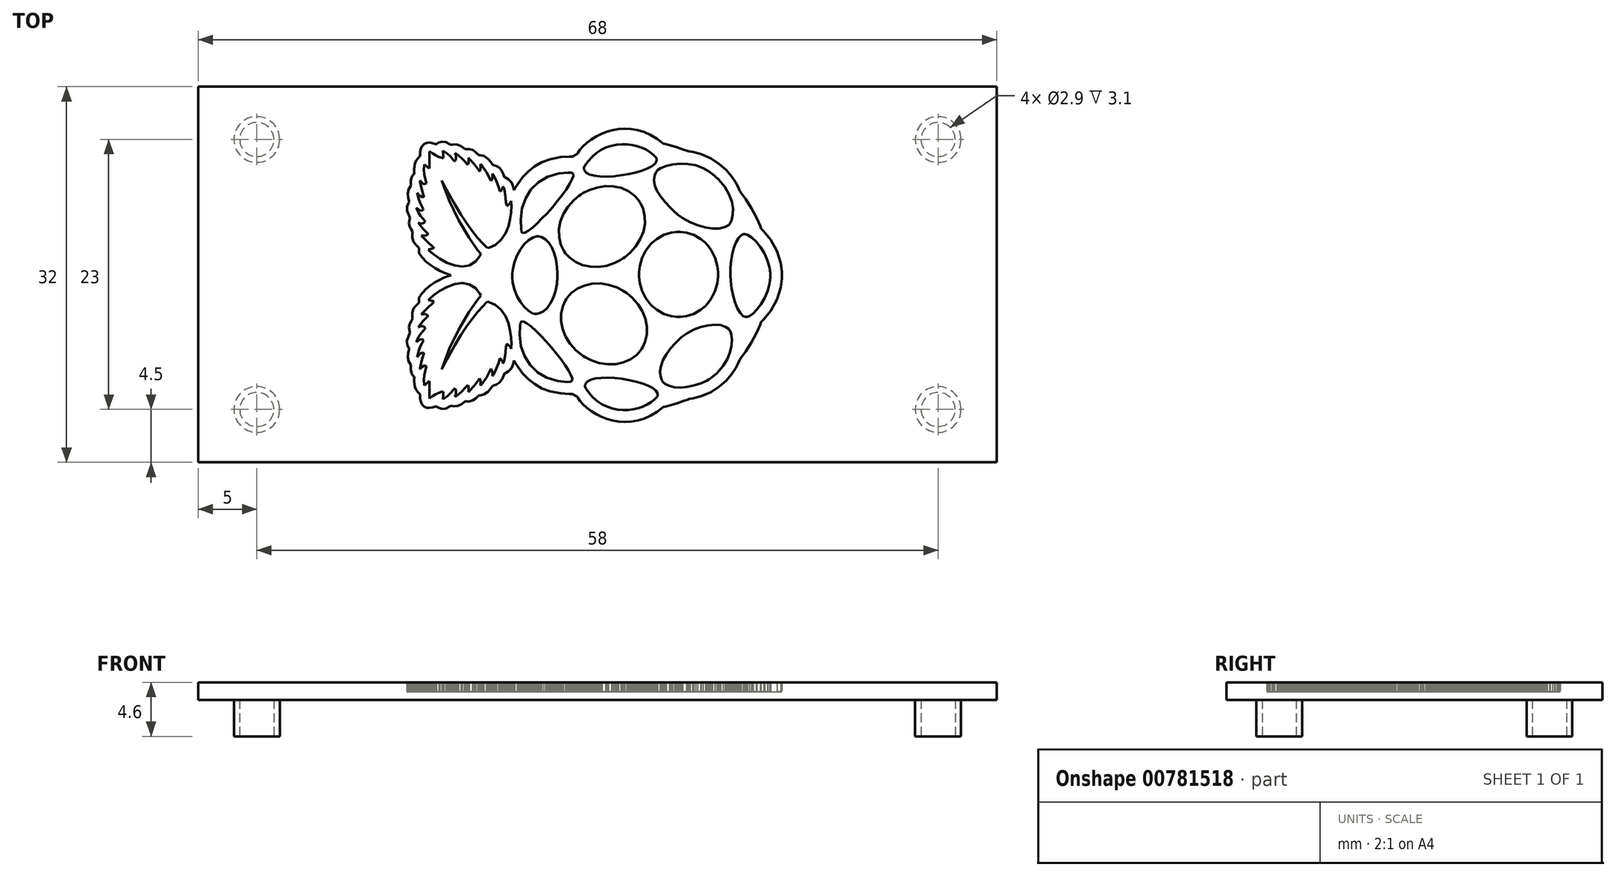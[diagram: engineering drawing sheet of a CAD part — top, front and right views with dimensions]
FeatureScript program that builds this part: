
annotation { "Feature Type Name" : "Feature", "Feature Type Description" : "" }
export const myFeature = defineFeature(function(context is Context, id is Id, definition is map)
    precondition{}
    {
        {
            var Q0;
            Q0=qCreatedBy(makeId("Top.planeOp"),FACE);
            var sketch = newSketch(context, id + "F0", { "sketchPlane" : qUnion([Q0])});
            skLineSegment(sketch, "E0.bottom", {"start": v(-34, 16) * mm, "end": v(34, 16) * mm});
            skLineSegment(sketch, "E0.top", {"start": v(-34, -16) * mm, "end": v(34, -16) * mm});
            skLineSegment(sketch, "E0.left", {"start": v(-34, 16) * mm, "end": v(-34, -16) * mm});
            skLineSegment(sketch, "E0.right", {"start": v(34, 16) * mm, "end": v(34, -16) * mm});
            skCircle(sketch, "E1", {"center": v(-29, 11.5) * mm, "radius": 1.45 * mm});
            skCircle(sketch, "E2", {"center": v(29, 11.5) * mm, "radius": 1.45 * mm});
            skCircle(sketch, "E3", {"center": v(29, -11.5) * mm, "radius": 1.45 * mm});
            skCircle(sketch, "E4", {"center": v(-29, -11.5) * mm, "radius": 1.45 * mm});
            skCircle(sketch, "E5", {"center": v(-29, 11.5) * mm, "radius": 1.95 * mm});
            skCircle(sketch, "E6", {"center": v(-29, -11.5) * mm, "radius": 1.95 * mm});
            skCircle(sketch, "E7", {"center": v(29, 11.5) * mm, "radius": 1.95 * mm});
            skCircle(sketch, "E8", {"center": v(29, -11.5) * mm, "radius": 1.95 * mm});
            skSolve(sketch);
        }
        {
            var Q0;
            Q0=qCreatedBy(makeId("Top.planeOp"),FACE);
            var sketch = newSketch(context, id + "F1", { "sketchPlane" : qUnion([Q0])});
            skLineSegment(sketch, "E9", {"start": v(-16.22, -5.8) * mm, "end": v(-16.22, -5.84) * mm});
            skLineSegment(sketch, "E10", {"start": v(-16.22, -5.84) * mm, "end": v(-16.17, -6.05) * mm});
            skLineSegment(sketch, "E11", {"start": v(-16.17, -6.05) * mm, "end": v(-16.04, -6.28) * mm});
            skLineSegment(sketch, "E12", {"start": v(-16.04, -6.28) * mm, "end": v(-16, -6.33) * mm});
            skLineSegment(sketch, "E13", {"start": v(-16, -6.33) * mm, "end": v(-16.04, -6.42) * mm});
            skLineSegment(sketch, "E14", {"start": v(-16.04, -6.42) * mm, "end": v(-16.12, -6.7) * mm});
            skLineSegment(sketch, "E15", {"start": v(-16.12, -6.7) * mm, "end": v(-16.15, -7.04) * mm});
            skLineSegment(sketch, "E16", {"start": v(-16.15, -7.04) * mm, "end": v(-16.08, -7.38) * mm});
            skLineSegment(sketch, "E17", {"start": v(-16.08, -7.38) * mm, "end": v(-15.94, -7.63) * mm});
            skLineSegment(sketch, "E18", {"start": v(-15.94, -7.63) * mm, "end": v(-15.87, -7.7) * mm});
            skLineSegment(sketch, "E19", {"start": v(-15.87, -7.7) * mm, "end": v(-15.89, -7.8) * mm});
            skLineSegment(sketch, "E20", {"start": v(-15.89, -7.8) * mm, "end": v(-15.9, -8.11) * mm});
            skLineSegment(sketch, "E21", {"start": v(-15.9, -8.11) * mm, "end": v(-15.84, -8.4) * mm});
            skLineSegment(sketch, "E22", {"start": v(-15.84, -8.4) * mm, "end": v(-15.73, -8.58) * mm});
            skLineSegment(sketch, "E23", {"start": v(-15.73, -8.58) * mm, "end": v(-15.62, -8.69) * mm});
            skLineSegment(sketch, "E24", {"start": v(-15.62, -8.69) * mm, "end": v(-15.58, -8.72) * mm});
            skLineSegment(sketch, "E25", {"start": v(-15.58, -8.72) * mm, "end": v(-15.58, -8.74) * mm});
            skLineSegment(sketch, "E26", {"start": v(-15.58, -8.74) * mm, "end": v(-15.59, -8.8) * mm});
            skLineSegment(sketch, "E27", {"start": v(-15.59, -8.8) * mm, "end": v(-15.6, -8.95) * mm});
            skLineSegment(sketch, "E28", {"start": v(-15.6, -8.95) * mm, "end": v(-15.6, -9.14) * mm});
            skLineSegment(sketch, "E29", {"start": v(-15.6, -9.14) * mm, "end": v(-15.58, -9.36) * mm});
            skLineSegment(sketch, "E30", {"start": v(-15.58, -9.36) * mm, "end": v(-15.53, -9.59) * mm});
            skLineSegment(sketch, "E31", {"start": v(-15.53, -9.59) * mm, "end": v(-15.44, -9.81) * mm});
            skLineSegment(sketch, "E32", {"start": v(-15.44, -9.81) * mm, "end": v(-15.3, -10.02) * mm});
            skLineSegment(sketch, "E33", {"start": v(-15.3, -10.02) * mm, "end": v(-15.16, -10.17) * mm});
            skLineSegment(sketch, "E34", {"start": v(-15.16, -10.17) * mm, "end": v(-15.1, -10.2) * mm});
            skLineSegment(sketch, "E35", {"start": v(-15.1, -10.2) * mm, "end": v(-15.11, -10.3) * mm});
            skLineSegment(sketch, "E36", {"start": v(-15.11, -10.3) * mm, "end": v(-15.1, -10.57) * mm});
            skLineSegment(sketch, "E37", {"start": v(-15.1, -10.57) * mm, "end": v(-15.04, -10.86) * mm});
            skLineSegment(sketch, "E38", {"start": v(-15.04, -10.86) * mm, "end": v(-14.92, -11.1) * mm});
            skLineSegment(sketch, "E39", {"start": v(-14.92, -11.1) * mm, "end": v(-14.75, -11.25) * mm});
            skLineSegment(sketch, "E40", {"start": v(-14.75, -11.25) * mm, "end": v(-14.54, -11.35) * mm});
            skLineSegment(sketch, "E41", {"start": v(-14.54, -11.35) * mm, "end": v(-14.3, -11.37) * mm});
            skLineSegment(sketch, "E42", {"start": v(-14.3, -11.37) * mm, "end": v(-14.04, -11.33) * mm});
            skLineSegment(sketch, "E43", {"start": v(-14.04, -11.33) * mm, "end": v(-13.84, -11.25) * mm});
            skLineSegment(sketch, "E44", {"start": v(-13.84, -11.25) * mm, "end": v(-13.78, -11.22) * mm});
            skLineSegment(sketch, "E45", {"start": v(-13.78, -11.22) * mm, "end": v(-13.71, -11.26) * mm});
            skLineSegment(sketch, "E46", {"start": v(-13.71, -11.26) * mm, "end": v(-13.52, -11.37) * mm});
            skLineSegment(sketch, "E47", {"start": v(-13.52, -11.37) * mm, "end": v(-13.24, -11.46) * mm});
            skLineSegment(sketch, "E48", {"start": v(-13.24, -11.46) * mm, "end": v(-12.9, -11.4) * mm});
            skLineSegment(sketch, "E49", {"start": v(-12.9, -11.4) * mm, "end": v(-12.57, -11.23) * mm});
            skLineSegment(sketch, "E50", {"start": v(-12.57, -11.23) * mm, "end": v(-12.47, -11.15) * mm});
            skLineSegment(sketch, "E51", {"start": v(-12.47, -11.15) * mm, "end": v(-12.4, -11.19) * mm});
            skLineSegment(sketch, "E52", {"start": v(-12.4, -11.19) * mm, "end": v(-12.2, -11.23) * mm});
            skLineSegment(sketch, "E53", {"start": v(-12.2, -11.23) * mm, "end": v(-11.9, -11.2) * mm});
            skLineSegment(sketch, "E54", {"start": v(-11.9, -11.2) * mm, "end": v(-11.6, -11.06) * mm});
            skLineSegment(sketch, "E55", {"start": v(-11.6, -11.06) * mm, "end": v(-11.34, -10.87) * mm});
            skLineSegment(sketch, "E56", {"start": v(-11.34, -10.87) * mm, "end": v(-11.26, -10.8) * mm});
            skLineSegment(sketch, "E57", {"start": v(-11.26, -10.8) * mm, "end": v(-11.18, -10.82) * mm});
            skLineSegment(sketch, "E58", {"start": v(-11.18, -10.82) * mm, "end": v(-10.91, -10.82) * mm});
            skLineSegment(sketch, "E59", {"start": v(-10.91, -10.82) * mm, "end": v(-10.61, -10.74) * mm});
            skLineSegment(sketch, "E60", {"start": v(-10.61, -10.74) * mm, "end": v(-10.35, -10.56) * mm});
            skLineSegment(sketch, "E61", {"start": v(-10.35, -10.56) * mm, "end": v(-10.18, -10.37) * mm});
            skLineSegment(sketch, "E62", {"start": v(-10.18, -10.37) * mm, "end": v(-10.13, -10.3) * mm});
            skLineSegment(sketch, "E63", {"start": v(-10.13, -10.3) * mm, "end": v(-10.02, -10.31) * mm});
            skLineSegment(sketch, "E64", {"start": v(-10.02, -10.31) * mm, "end": v(-9.67, -10.23) * mm});
            skLineSegment(sketch, "E65", {"start": v(-9.67, -10.23) * mm, "end": v(-9.32, -9.99) * mm});
            skLineSegment(sketch, "E66", {"start": v(-9.32, -9.99) * mm, "end": v(-9.06, -9.7) * mm});
            skLineSegment(sketch, "E67", {"start": v(-9.06, -9.7) * mm, "end": v(-8.94, -9.51) * mm});
            skLineSegment(sketch, "E68", {"start": v(-8.94, -9.51) * mm, "end": v(-8.9, -9.46) * mm});
            skLineSegment(sketch, "E69", {"start": v(-8.9, -9.46) * mm, "end": v(-8.83, -9.45) * mm});
            skLineSegment(sketch, "E70", {"start": v(-8.83, -9.45) * mm, "end": v(-8.61, -9.38) * mm});
            skLineSegment(sketch, "E71", {"start": v(-8.61, -9.38) * mm, "end": v(-8.34, -9.2) * mm});
            skLineSegment(sketch, "E72", {"start": v(-8.34, -9.2) * mm, "end": v(-8.1, -8.9) * mm});
            skLineSegment(sketch, "E73", {"start": v(-8.1, -8.9) * mm, "end": v(-7.96, -8.54) * mm});
            skLineSegment(sketch, "E74", {"start": v(-7.96, -8.54) * mm, "end": v(-7.92, -8.41) * mm});
            skLineSegment(sketch, "E75", {"start": v(-7.92, -8.41) * mm, "end": v(-7.83, -8.4) * mm});
            skLineSegment(sketch, "E76", {"start": v(-7.83, -8.4) * mm, "end": v(-7.56, -8.25) * mm});
            skLineSegment(sketch, "E77", {"start": v(-7.56, -8.25) * mm, "end": v(-7.33, -8) * mm});
            skLineSegment(sketch, "E78", {"start": v(-7.33, -8) * mm, "end": v(-7.2, -7.68) * mm});
            skLineSegment(sketch, "E79", {"start": v(-7.2, -7.68) * mm, "end": v(-7.12, -7.42) * mm});
            skLineSegment(sketch, "E80", {"start": v(-7.12, -7.42) * mm, "end": v(-7.1, -7.33) * mm});
            skLineSegment(sketch, "E81", {"start": v(-7.1, -7.33) * mm, "end": v(-7.02, -7.48) * mm});
            skLineSegment(sketch, "E82", {"start": v(-7.02, -7.48) * mm, "end": v(-6.75, -7.9) * mm});
            skLineSegment(sketch, "E83", {"start": v(-6.75, -7.9) * mm, "end": v(-6.35, -8.43) * mm});
            skLineSegment(sketch, "E84", {"start": v(-6.35, -8.43) * mm, "end": v(-5.9, -8.92) * mm});
            skLineSegment(sketch, "E85", {"start": v(-5.9, -8.92) * mm, "end": v(-5.36, -9.34) * mm});
            skLineSegment(sketch, "E86", {"start": v(-5.36, -9.34) * mm, "end": v(-4.74, -9.7) * mm});
            skLineSegment(sketch, "E87", {"start": v(-4.74, -9.7) * mm, "end": v(-4, -9.96) * mm});
            skLineSegment(sketch, "E88", {"start": v(-4, -9.96) * mm, "end": v(-3.14, -10.13) * mm});
            skLineSegment(sketch, "E89", {"start": v(-3.14, -10.13) * mm, "end": v(-2.38, -10.19) * mm});
            skLineSegment(sketch, "E90", {"start": v(-2.38, -10.19) * mm, "end": v(-2.13, -10.19) * mm});
            skLineSegment(sketch, "E91", {"start": v(-2.13, -10.19) * mm, "end": v(-1.73, -10.41) * mm});
            skLineSegment(sketch, "E92", {"start": v(-1.73, -10.41) * mm, "end": v(-1.68, -10.5) * mm});
            skLineSegment(sketch, "E93", {"start": v(-1.68, -10.5) * mm, "end": v(-1.5, -10.74) * mm});
            skLineSegment(sketch, "E94", {"start": v(-1.5, -10.74) * mm, "end": v(-1.22, -11.06) * mm});
            skLineSegment(sketch, "E95", {"start": v(-1.22, -11.06) * mm, "end": v(-0.9, -11.36) * mm});
            skLineSegment(sketch, "E96", {"start": v(-0.9, -11.36) * mm, "end": v(-0.52, -11.64) * mm});
            skLineSegment(sketch, "E97", {"start": v(-0.52, -11.64) * mm, "end": v(-0.12, -11.9) * mm});
            skLineSegment(sketch, "E98", {"start": v(-0.12, -11.9) * mm, "end": v(0.33, -12.12) * mm});
            skLineSegment(sketch, "E99", {"start": v(0.33, -12.12) * mm, "end": v(0.8, -12.3) * mm});
            skLineSegment(sketch, "E100", {"start": v(0.8, -12.3) * mm, "end": v(1.3, -12.44) * mm});
            skLineSegment(sketch, "E101", {"start": v(1.3, -12.44) * mm, "end": v(1.8, -12.53) * mm});
            skLineSegment(sketch, "E102", {"start": v(1.8, -12.53) * mm, "end": v(2.34, -12.57) * mm});
            skLineSegment(sketch, "E103", {"start": v(2.34, -12.57) * mm, "end": v(2.88, -12.54) * mm});
            skLineSegment(sketch, "E104", {"start": v(2.88, -12.54) * mm, "end": v(3.43, -12.45) * mm});
            skLineSegment(sketch, "E105", {"start": v(3.43, -12.45) * mm, "end": v(3.98, -12.28) * mm});
            skLineSegment(sketch, "E106", {"start": v(3.98, -12.28) * mm, "end": v(4.53, -12.03) * mm});
            skLineSegment(sketch, "E107", {"start": v(4.53, -12.03) * mm, "end": v(5.08, -11.7) * mm});
            skLineSegment(sketch, "E108", {"start": v(5.08, -11.7) * mm, "end": v(5.48, -11.4) * mm});
            skLineSegment(sketch, "E109", {"start": v(5.48, -11.4) * mm, "end": v(5.61, -11.28) * mm});
            skLineSegment(sketch, "E110", {"start": v(5.61, -11.28) * mm, "end": v(5.77, -11.26) * mm});
            skLineSegment(sketch, "E111", {"start": v(5.77, -11.26) * mm, "end": v(6.23, -11.14) * mm});
            skLineSegment(sketch, "E112", {"start": v(6.23, -11.14) * mm, "end": v(6.78, -10.98) * mm});
            skLineSegment(sketch, "E113", {"start": v(6.78, -10.98) * mm, "end": v(7.3, -10.8) * mm});
            skLineSegment(sketch, "E114", {"start": v(7.3, -10.8) * mm, "end": v(7.69, -10.65) * mm});
            skLineSegment(sketch, "E115", {"start": v(7.69, -10.65) * mm, "end": v(7.82, -10.6) * mm});
            skLineSegment(sketch, "E116", {"start": v(7.82, -10.6) * mm, "end": v(8.07, -10.57) * mm});
            skLineSegment(sketch, "E117", {"start": v(8.07, -10.57) * mm, "end": v(8.8, -10.38) * mm});
            skLineSegment(sketch, "E118", {"start": v(8.8, -10.38) * mm, "end": v(9.66, -10.02) * mm});
            skLineSegment(sketch, "E119", {"start": v(9.66, -10.02) * mm, "end": v(10.37, -9.55) * mm});
            skLineSegment(sketch, "E120", {"start": v(10.37, -9.55) * mm, "end": v(10.96, -9.03) * mm});
            skLineSegment(sketch, "E121", {"start": v(10.96, -9.03) * mm, "end": v(11.43, -8.5) * mm});
            skLineSegment(sketch, "E122", {"start": v(11.43, -8.5) * mm, "end": v(11.77, -7.99) * mm});
            skLineSegment(sketch, "E123", {"start": v(11.77, -7.99) * mm, "end": v(12, -7.56) * mm});
            skLineSegment(sketch, "E124", {"start": v(12, -7.56) * mm, "end": v(12.1, -7.33) * mm});
            skLineSegment(sketch, "E125", {"start": v(12.1, -7.33) * mm, "end": v(12.11, -7.25) * mm});
            skLineSegment(sketch, "E126", {"start": v(12.11, -7.25) * mm, "end": v(12.24, -7.08) * mm});
            skLineSegment(sketch, "E127", {"start": v(12.24, -7.08) * mm, "end": v(12.62, -6.55) * mm});
            skLineSegment(sketch, "E128", {"start": v(12.62, -6.55) * mm, "end": v(13.1, -5.8) * mm});
            skLineSegment(sketch, "E129", {"start": v(13.1, -5.8) * mm, "end": v(13.55, -4.97) * mm});
            skLineSegment(sketch, "E130", {"start": v(13.55, -4.97) * mm, "end": v(13.85, -4.28) * mm});
            skLineSegment(sketch, "E131", {"start": v(13.85, -4.28) * mm, "end": v(13.93, -4.04) * mm});
            skLineSegment(sketch, "E132", {"start": v(13.93, -4.04) * mm, "end": v(14.16, -3.83) * mm});
            skLineSegment(sketch, "E133", {"start": v(14.16, -3.83) * mm, "end": v(14.75, -3.1) * mm});
            skLineSegment(sketch, "E134", {"start": v(14.75, -3.1) * mm, "end": v(15.3, -2.11) * mm});
            skLineSegment(sketch, "E135", {"start": v(15.3, -2.11) * mm, "end": v(15.6, -1.11) * mm});
            skLineSegment(sketch, "E136", {"start": v(15.6, -1.11) * mm, "end": v(15.7, -0.35) * mm});
            skLineSegment(sketch, "E137", {"start": v(15.7, -0.35) * mm, "end": v(15.7, -0.1) * mm});
            skLineSegment(sketch, "E138", {"start": v(15.7, -0.1) * mm, "end": v(15.7, -0.08) * mm});
            skLineSegment(sketch, "E139", {"start": v(15.7, -0.08) * mm, "end": v(15.7, -0.04) * mm});
            skLineSegment(sketch, "E140", {"start": v(15.7, -0.04) * mm, "end": v(15.7, -0.04) * mm});
            skLineSegment(sketch, "E141", {"start": v(15.7, -0.04) * mm, "end": v(15.7, 0.22) * mm});
            skLineSegment(sketch, "E142", {"start": v(15.7, 0.22) * mm, "end": v(15.6, 0.98) * mm});
            skLineSegment(sketch, "E143", {"start": v(15.6, 0.98) * mm, "end": v(15.3, 1.98) * mm});
            skLineSegment(sketch, "E144", {"start": v(15.3, 1.98) * mm, "end": v(14.75, 2.96) * mm});
            skLineSegment(sketch, "E145", {"start": v(14.75, 2.96) * mm, "end": v(14.16, 3.7) * mm});
            skLineSegment(sketch, "E146", {"start": v(14.16, 3.7) * mm, "end": v(13.93, 3.9) * mm});
            skLineSegment(sketch, "E147", {"start": v(13.93, 3.9) * mm, "end": v(13.85, 4.14) * mm});
            skLineSegment(sketch, "E148", {"start": v(13.85, 4.14) * mm, "end": v(13.55, 4.84) * mm});
            skLineSegment(sketch, "E149", {"start": v(13.55, 4.84) * mm, "end": v(13.1, 5.66) * mm});
            skLineSegment(sketch, "E150", {"start": v(13.1, 5.66) * mm, "end": v(12.62, 6.41) * mm});
            skLineSegment(sketch, "E151", {"start": v(12.62, 6.41) * mm, "end": v(12.24, 6.94) * mm});
            skLineSegment(sketch, "E152", {"start": v(12.24, 6.94) * mm, "end": v(12.11, 7.12) * mm});
            skLineSegment(sketch, "E153", {"start": v(12.11, 7.12) * mm, "end": v(12.1, 7.2) * mm});
            skLineSegment(sketch, "E154", {"start": v(12.1, 7.2) * mm, "end": v(12, 7.42) * mm});
            skLineSegment(sketch, "E155", {"start": v(12, 7.42) * mm, "end": v(11.77, 7.85) * mm});
            skLineSegment(sketch, "E156", {"start": v(11.77, 7.85) * mm, "end": v(11.43, 8.36) * mm});
            skLineSegment(sketch, "E157", {"start": v(11.43, 8.36) * mm, "end": v(10.96, 8.9) * mm});
            skLineSegment(sketch, "E158", {"start": v(10.96, 8.9) * mm, "end": v(10.37, 9.42) * mm});
            skLineSegment(sketch, "E159", {"start": v(10.37, 9.42) * mm, "end": v(9.66, 9.88) * mm});
            skLineSegment(sketch, "E160", {"start": v(9.66, 9.88) * mm, "end": v(8.8, 10.25) * mm});
            skLineSegment(sketch, "E161", {"start": v(8.8, 10.25) * mm, "end": v(8.07, 10.44) * mm});
            skLineSegment(sketch, "E162", {"start": v(8.07, 10.44) * mm, "end": v(7.82, 10.47) * mm});
            skLineSegment(sketch, "E163", {"start": v(7.82, 10.47) * mm, "end": v(7.69, 10.52) * mm});
            skLineSegment(sketch, "E164", {"start": v(7.69, 10.52) * mm, "end": v(7.3, 10.66) * mm});
            skLineSegment(sketch, "E165", {"start": v(7.3, 10.66) * mm, "end": v(6.78, 10.84) * mm});
            skLineSegment(sketch, "E166", {"start": v(6.78, 10.84) * mm, "end": v(6.23, 11) * mm});
            skLineSegment(sketch, "E167", {"start": v(6.23, 11) * mm, "end": v(5.77, 11.12) * mm});
            skLineSegment(sketch, "E168", {"start": v(5.77, 11.12) * mm, "end": v(5.61, 11.15) * mm});
            skLineSegment(sketch, "E169", {"start": v(5.61, 11.15) * mm, "end": v(5.48, 11.26) * mm});
            skLineSegment(sketch, "E170", {"start": v(5.48, 11.26) * mm, "end": v(5.08, 11.57) * mm});
            skLineSegment(sketch, "E171", {"start": v(5.08, 11.57) * mm, "end": v(4.53, 11.9) * mm});
            skLineSegment(sketch, "E172", {"start": v(4.53, 11.9) * mm, "end": v(3.98, 12.14) * mm});
            skLineSegment(sketch, "E173", {"start": v(3.98, 12.14) * mm, "end": v(3.43, 12.31) * mm});
            skLineSegment(sketch, "E174", {"start": v(3.43, 12.31) * mm, "end": v(2.88, 12.4) * mm});
            skLineSegment(sketch, "E175", {"start": v(2.88, 12.4) * mm, "end": v(2.34, 12.43) * mm});
            skLineSegment(sketch, "E176", {"start": v(2.34, 12.43) * mm, "end": v(1.8, 12.4) * mm});
            skLineSegment(sketch, "E177", {"start": v(1.8, 12.4) * mm, "end": v(1.3, 12.3) * mm});
            skLineSegment(sketch, "E178", {"start": v(1.3, 12.3) * mm, "end": v(0.8, 12.17) * mm});
            skLineSegment(sketch, "E179", {"start": v(0.8, 12.17) * mm, "end": v(0.32, 11.99) * mm});
            skLineSegment(sketch, "E180", {"start": v(0.32, 11.99) * mm, "end": v(-0.12, 11.76) * mm});
            skLineSegment(sketch, "E181", {"start": v(-0.12, 11.76) * mm, "end": v(-0.52, 11.5) * mm});
            skLineSegment(sketch, "E182", {"start": v(-0.52, 11.5) * mm, "end": v(-0.9, 11.23) * mm});
            skLineSegment(sketch, "E183", {"start": v(-0.9, 11.23) * mm, "end": v(-1.22, 10.92) * mm});
            skLineSegment(sketch, "E184", {"start": v(-1.22, 10.92) * mm, "end": v(-1.5, 10.6) * mm});
            skLineSegment(sketch, "E185", {"start": v(-1.5, 10.6) * mm, "end": v(-1.68, 10.36) * mm});
            skLineSegment(sketch, "E186", {"start": v(-1.68, 10.36) * mm, "end": v(-1.73, 10.28) * mm});
            skLineSegment(sketch, "E187", {"start": v(-1.73, 10.28) * mm, "end": v(-2.13, 10.05) * mm});
            skLineSegment(sketch, "E188", {"start": v(-2.13, 10.05) * mm, "end": v(-2.38, 10.05) * mm});
            skLineSegment(sketch, "E189", {"start": v(-2.38, 10.05) * mm, "end": v(-3.14, 10) * mm});
            skLineSegment(sketch, "E190", {"start": v(-3.14, 10) * mm, "end": v(-4, 9.83) * mm});
            skLineSegment(sketch, "E191", {"start": v(-4, 9.83) * mm, "end": v(-4.74, 9.56) * mm});
            skLineSegment(sketch, "E192", {"start": v(-4.74, 9.56) * mm, "end": v(-5.36, 9.2) * mm});
            skLineSegment(sketch, "E193", {"start": v(-5.36, 9.2) * mm, "end": v(-5.9, 8.78) * mm});
            skLineSegment(sketch, "E194", {"start": v(-5.9, 8.78) * mm, "end": v(-6.35, 8.3) * mm});
            skLineSegment(sketch, "E195", {"start": v(-6.35, 8.3) * mm, "end": v(-6.75, 7.76) * mm});
            skLineSegment(sketch, "E196", {"start": v(-6.75, 7.76) * mm, "end": v(-7.02, 7.34) * mm});
            skLineSegment(sketch, "E197", {"start": v(-7.02, 7.34) * mm, "end": v(-7.1, 7.2) * mm});
            skLineSegment(sketch, "E198", {"start": v(-7.1, 7.2) * mm, "end": v(-7.12, 7.28) * mm});
            skLineSegment(sketch, "E199", {"start": v(-7.12, 7.28) * mm, "end": v(-7.2, 7.54) * mm});
            skLineSegment(sketch, "E200", {"start": v(-7.2, 7.54) * mm, "end": v(-7.34, 7.86) * mm});
            skLineSegment(sketch, "E201", {"start": v(-7.34, 7.86) * mm, "end": v(-7.56, 8.12) * mm});
            skLineSegment(sketch, "E202", {"start": v(-7.56, 8.12) * mm, "end": v(-7.83, 8.26) * mm});
            skLineSegment(sketch, "E203", {"start": v(-7.83, 8.26) * mm, "end": v(-7.92, 8.28) * mm});
            skLineSegment(sketch, "E204", {"start": v(-7.92, 8.28) * mm, "end": v(-7.96, 8.4) * mm});
            skLineSegment(sketch, "E205", {"start": v(-7.96, 8.4) * mm, "end": v(-8.1, 8.77) * mm});
            skLineSegment(sketch, "E206", {"start": v(-8.1, 8.77) * mm, "end": v(-8.34, 9.07) * mm});
            skLineSegment(sketch, "E207", {"start": v(-8.34, 9.07) * mm, "end": v(-8.61, 9.24) * mm});
            skLineSegment(sketch, "E208", {"start": v(-8.61, 9.24) * mm, "end": v(-8.83, 9.31) * mm});
            skLineSegment(sketch, "E209", {"start": v(-8.83, 9.31) * mm, "end": v(-8.9, 9.33) * mm});
            skLineSegment(sketch, "E210", {"start": v(-8.9, 9.33) * mm, "end": v(-8.94, 9.38) * mm});
            skLineSegment(sketch, "E211", {"start": v(-8.94, 9.38) * mm, "end": v(-9.06, 9.56) * mm});
            skLineSegment(sketch, "E212", {"start": v(-9.06, 9.56) * mm, "end": v(-9.32, 9.85) * mm});
            skLineSegment(sketch, "E213", {"start": v(-9.32, 9.85) * mm, "end": v(-9.67, 10.1) * mm});
            skLineSegment(sketch, "E214", {"start": v(-9.67, 10.1) * mm, "end": v(-10.02, 10.18) * mm});
            skLineSegment(sketch, "E215", {"start": v(-10.02, 10.18) * mm, "end": v(-10.13, 10.16) * mm});
            skLineSegment(sketch, "E216", {"start": v(-10.13, 10.16) * mm, "end": v(-10.18, 10.23) * mm});
            skLineSegment(sketch, "E217", {"start": v(-10.18, 10.23) * mm, "end": v(-10.35, 10.42) * mm});
            skLineSegment(sketch, "E218", {"start": v(-10.35, 10.42) * mm, "end": v(-10.61, 10.6) * mm});
            skLineSegment(sketch, "E219", {"start": v(-10.61, 10.6) * mm, "end": v(-10.91, 10.69) * mm});
            skLineSegment(sketch, "E220", {"start": v(-10.91, 10.69) * mm, "end": v(-11.18, 10.68) * mm});
            skLineSegment(sketch, "E221", {"start": v(-11.18, 10.68) * mm, "end": v(-11.26, 10.67) * mm});
            skLineSegment(sketch, "E222", {"start": v(-11.26, 10.67) * mm, "end": v(-11.34, 10.74) * mm});
            skLineSegment(sketch, "E223", {"start": v(-11.34, 10.74) * mm, "end": v(-11.6, 10.92) * mm});
            skLineSegment(sketch, "E224", {"start": v(-11.6, 10.92) * mm, "end": v(-11.9, 11.07) * mm});
            skLineSegment(sketch, "E225", {"start": v(-11.9, 11.07) * mm, "end": v(-12.2, 11.1) * mm});
            skLineSegment(sketch, "E226", {"start": v(-12.2, 11.1) * mm, "end": v(-12.4, 11.05) * mm});
            skLineSegment(sketch, "E227", {"start": v(-12.4, 11.05) * mm, "end": v(-12.47, 11.02) * mm});
            skLineSegment(sketch, "E228", {"start": v(-12.47, 11.02) * mm, "end": v(-12.57, 11.1) * mm});
            skLineSegment(sketch, "E229", {"start": v(-12.57, 11.1) * mm, "end": v(-12.9, 11.27) * mm});
            skLineSegment(sketch, "E230", {"start": v(-12.9, 11.27) * mm, "end": v(-13.24, 11.32) * mm});
            skLineSegment(sketch, "E231", {"start": v(-13.24, 11.32) * mm, "end": v(-13.52, 11.24) * mm});
            skLineSegment(sketch, "E232", {"start": v(-13.52, 11.24) * mm, "end": v(-13.71, 11.12) * mm});
            skLineSegment(sketch, "E233", {"start": v(-13.71, 11.12) * mm, "end": v(-13.78, 11.08) * mm});
            skLineSegment(sketch, "E234", {"start": v(-13.78, 11.08) * mm, "end": v(-13.84, 11.12) * mm});
            skLineSegment(sketch, "E235", {"start": v(-13.84, 11.12) * mm, "end": v(-14.04, 11.2) * mm});
            skLineSegment(sketch, "E236", {"start": v(-14.04, 11.2) * mm, "end": v(-14.3, 11.24) * mm});
            skLineSegment(sketch, "E237", {"start": v(-14.3, 11.24) * mm, "end": v(-14.54, 11.2) * mm});
            skLineSegment(sketch, "E238", {"start": v(-14.54, 11.2) * mm, "end": v(-14.75, 11.12) * mm});
            skLineSegment(sketch, "E239", {"start": v(-14.75, 11.12) * mm, "end": v(-14.92, 10.96) * mm});
            skLineSegment(sketch, "E240", {"start": v(-14.92, 10.96) * mm, "end": v(-15.04, 10.73) * mm});
            skLineSegment(sketch, "E241", {"start": v(-15.04, 10.73) * mm, "end": v(-15.1, 10.43) * mm});
            skLineSegment(sketch, "E242", {"start": v(-15.1, 10.43) * mm, "end": v(-15.11, 10.16) * mm});
            skLineSegment(sketch, "E243", {"start": v(-15.11, 10.16) * mm, "end": v(-15.1, 10.07) * mm});
            skLineSegment(sketch, "E244", {"start": v(-15.1, 10.07) * mm, "end": v(-15.16, 10.03) * mm});
            skLineSegment(sketch, "E245", {"start": v(-15.16, 10.03) * mm, "end": v(-15.3, 9.89) * mm});
            skLineSegment(sketch, "E246", {"start": v(-15.3, 9.89) * mm, "end": v(-15.44, 9.68) * mm});
            skLineSegment(sketch, "E247", {"start": v(-15.44, 9.68) * mm, "end": v(-15.53, 9.45) * mm});
            skLineSegment(sketch, "E248", {"start": v(-15.53, 9.45) * mm, "end": v(-15.58, 9.22) * mm});
            skLineSegment(sketch, "E249", {"start": v(-15.58, 9.22) * mm, "end": v(-15.6, 9) * mm});
            skLineSegment(sketch, "E250", {"start": v(-15.6, 9) * mm, "end": v(-15.6, 8.82) * mm});
            skLineSegment(sketch, "E251", {"start": v(-15.6, 8.82) * mm, "end": v(-15.59, 8.67) * mm});
            skLineSegment(sketch, "E252", {"start": v(-15.59, 8.67) * mm, "end": v(-15.58, 8.6) * mm});
            skLineSegment(sketch, "E253", {"start": v(-15.58, 8.6) * mm, "end": v(-15.58, 8.58) * mm});
            skLineSegment(sketch, "E254", {"start": v(-15.58, 8.58) * mm, "end": v(-15.62, 8.55) * mm});
            skLineSegment(sketch, "E255", {"start": v(-15.62, 8.55) * mm, "end": v(-15.73, 8.45) * mm});
            skLineSegment(sketch, "E256", {"start": v(-15.73, 8.45) * mm, "end": v(-15.84, 8.26) * mm});
            skLineSegment(sketch, "E257", {"start": v(-15.84, 8.26) * mm, "end": v(-15.9, 7.98) * mm});
            skLineSegment(sketch, "E258", {"start": v(-15.9, 7.98) * mm, "end": v(-15.89, 7.67) * mm});
            skLineSegment(sketch, "E259", {"start": v(-15.89, 7.67) * mm, "end": v(-15.87, 7.57) * mm});
            skLineSegment(sketch, "E260", {"start": v(-15.87, 7.57) * mm, "end": v(-15.94, 7.5) * mm});
            skLineSegment(sketch, "E261", {"start": v(-15.94, 7.5) * mm, "end": v(-16.08, 7.24) * mm});
            skLineSegment(sketch, "E262", {"start": v(-16.08, 7.24) * mm, "end": v(-16.15, 6.9) * mm});
            skLineSegment(sketch, "E263", {"start": v(-16.15, 6.9) * mm, "end": v(-16.12, 6.56) * mm});
            skLineSegment(sketch, "E264", {"start": v(-16.12, 6.56) * mm, "end": v(-16.04, 6.28) * mm});
            skLineSegment(sketch, "E265", {"start": v(-16.04, 6.28) * mm, "end": v(-16, 6.2) * mm});
            skLineSegment(sketch, "E266", {"start": v(-16, 6.2) * mm, "end": v(-16.07, 6.11) * mm});
            skLineSegment(sketch, "E267", {"start": v(-16.07, 6.11) * mm, "end": v(-16.2, 5.8) * mm});
            skLineSegment(sketch, "E268", {"start": v(-16.2, 5.8) * mm, "end": v(-16.2, 5.45) * mm});
            skLineSegment(sketch, "E269", {"start": v(-16.2, 5.45) * mm, "end": v(-16.08, 5.13) * mm});
            skLineSegment(sketch, "E270", {"start": v(-16.08, 5.13) * mm, "end": v(-15.98, 4.9) * mm});
            skLineSegment(sketch, "E271", {"start": v(-15.98, 4.9) * mm, "end": v(-15.96, 4.81) * mm});
            skLineSegment(sketch, "E272", {"start": v(-15.96, 4.81) * mm, "end": v(-15.99, 4.7) * mm});
            skLineSegment(sketch, "E273", {"start": v(-15.99, 4.7) * mm, "end": v(-16.04, 4.38) * mm});
            skLineSegment(sketch, "E274", {"start": v(-16.04, 4.38) * mm, "end": v(-15.98, 4.08) * mm});
            skLineSegment(sketch, "E275", {"start": v(-15.98, 4.08) * mm, "end": v(-15.86, 3.85) * mm});
            skLineSegment(sketch, "E276", {"start": v(-15.86, 3.85) * mm, "end": v(-15.77, 3.68) * mm});
            skLineSegment(sketch, "E277", {"start": v(-15.77, 3.68) * mm, "end": v(-15.75, 3.62) * mm});
            skLineSegment(sketch, "E278", {"start": v(-15.75, 3.62) * mm, "end": v(-15.77, 3.5) * mm});
            skLineSegment(sketch, "E279", {"start": v(-15.77, 3.5) * mm, "end": v(-15.78, 3.14) * mm});
            skLineSegment(sketch, "E280", {"start": v(-15.78, 3.14) * mm, "end": v(-15.67, 2.8) * mm});
            skLineSegment(sketch, "E281", {"start": v(-15.67, 2.8) * mm, "end": v(-15.45, 2.52) * mm});
            skLineSegment(sketch, "E282", {"start": v(-15.45, 2.52) * mm, "end": v(-15.25, 2.33) * mm});
            skLineSegment(sketch, "E283", {"start": v(-15.25, 2.33) * mm, "end": v(-15.19, 2.27) * mm});
            skLineSegment(sketch, "E284", {"start": v(-15.19, 2.27) * mm, "end": v(-15.2, 1.84) * mm});
            skLineSegment(sketch, "E285", {"start": v(-15.2, 1.84) * mm, "end": v(-15.14, 1.74) * mm});
            skLineSegment(sketch, "E286", {"start": v(-15.14, 1.74) * mm, "end": v(-14.92, 1.44) * mm});
            skLineSegment(sketch, "E287", {"start": v(-14.92, 1.44) * mm, "end": v(-14.58, 1.1) * mm});
            skLineSegment(sketch, "E288", {"start": v(-14.58, 1.1) * mm, "end": v(-14.22, 0.79) * mm});
            skLineSegment(sketch, "E289", {"start": v(-14.22, 0.79) * mm, "end": v(-13.83, 0.53) * mm});
            skLineSegment(sketch, "E290", {"start": v(-13.83, 0.53) * mm, "end": v(-13.45, 0.32) * mm});
            skLineSegment(sketch, "E291", {"start": v(-13.45, 0.32) * mm, "end": v(-13.08, 0.15) * mm});
            skLineSegment(sketch, "E292", {"start": v(-13.08, 0.15) * mm, "end": v(-12.74, 0.02) * mm});
            skLineSegment(sketch, "E293", {"start": v(-12.74, 0.02) * mm, "end": v(-12.52, -0.05) * mm});
            skLineSegment(sketch, "E294", {"start": v(-12.52, -0.05) * mm, "end": v(-12.45, -0.07) * mm});
            skLineSegment(sketch, "E295", {"start": v(-12.45, -0.07) * mm, "end": v(-12.52, -0.09) * mm});
            skLineSegment(sketch, "E296", {"start": v(-12.52, -0.09) * mm, "end": v(-12.74, -0.16) * mm});
            skLineSegment(sketch, "E297", {"start": v(-12.74, -0.16) * mm, "end": v(-13.08, -0.3) * mm});
            skLineSegment(sketch, "E298", {"start": v(-13.08, -0.3) * mm, "end": v(-13.45, -0.46) * mm});
            skLineSegment(sketch, "E299", {"start": v(-13.45, -0.46) * mm, "end": v(-13.83, -0.67) * mm});
            skLineSegment(sketch, "E300", {"start": v(-13.83, -0.67) * mm, "end": v(-14.22, -0.93) * mm});
            skLineSegment(sketch, "E301", {"start": v(-14.22, -0.93) * mm, "end": v(-14.58, -1.23) * mm});
            skLineSegment(sketch, "E302", {"start": v(-14.58, -1.23) * mm, "end": v(-14.92, -1.58) * mm});
            skLineSegment(sketch, "E303", {"start": v(-14.92, -1.58) * mm, "end": v(-15.14, -1.87) * mm});
            skLineSegment(sketch, "E304", {"start": v(-15.14, -1.87) * mm, "end": v(-15.2, -1.98) * mm});
            skLineSegment(sketch, "E305", {"start": v(-15.2, -1.98) * mm, "end": v(-15.19, -2.4) * mm});
            skLineSegment(sketch, "E306", {"start": v(-15.19, -2.4) * mm, "end": v(-15.25, -2.47) * mm});
            skLineSegment(sketch, "E307", {"start": v(-15.25, -2.47) * mm, "end": v(-15.45, -2.66) * mm});
            skLineSegment(sketch, "E308", {"start": v(-15.45, -2.66) * mm, "end": v(-15.67, -2.93) * mm});
            skLineSegment(sketch, "E309", {"start": v(-15.67, -2.93) * mm, "end": v(-15.78, -3.27) * mm});
            skLineSegment(sketch, "E310", {"start": v(-15.78, -3.27) * mm, "end": v(-15.77, -3.64) * mm});
            skLineSegment(sketch, "E311", {"start": v(-15.77, -3.64) * mm, "end": v(-15.75, -3.75) * mm});
            skLineSegment(sketch, "E312", {"start": v(-15.75, -3.75) * mm, "end": v(-15.77, -3.81) * mm});
            skLineSegment(sketch, "E313", {"start": v(-15.77, -3.81) * mm, "end": v(-15.86, -3.98) * mm});
            skLineSegment(sketch, "E314", {"start": v(-15.86, -3.98) * mm, "end": v(-15.98, -4.22) * mm});
            skLineSegment(sketch, "E315", {"start": v(-15.98, -4.22) * mm, "end": v(-16.04, -4.51) * mm});
            skLineSegment(sketch, "E316", {"start": v(-16.04, -4.51) * mm, "end": v(-15.99, -4.84) * mm});
            skLineSegment(sketch, "E317", {"start": v(-15.99, -4.84) * mm, "end": v(-15.96, -4.95) * mm});
            skLineSegment(sketch, "E318", {"start": v(-15.96, -4.95) * mm, "end": v(-15.97, -5) * mm});
            skLineSegment(sketch, "E319", {"start": v(-15.97, -5) * mm, "end": v(-16.04, -5.16) * mm});
            skLineSegment(sketch, "E320", {"start": v(-16.04, -5.16) * mm, "end": v(-16.13, -5.36) * mm});
            skLineSegment(sketch, "E321", {"start": v(-16.13, -5.36) * mm, "end": v(-16.2, -5.58) * mm});
            skLineSegment(sketch, "E322", {"start": v(-16.2, -5.58) * mm, "end": v(-16.23, -5.74) * mm});
            skLineSegment(sketch, "E323", {"start": v(-16.23, -5.74) * mm, "end": v(-16.22, -5.8) * mm});
            skLineSegment(sketch, "E324", {"start": v(-16.22, -5.8) * mm, "end": v(-16.22, -5.8) * mm});
            skLineSegment(sketch, "E325", {"start": v(-13.26, -8.07) * mm, "end": v(-13.12, -7.8) * mm});
            skLineSegment(sketch, "E326", {"start": v(-13.12, -7.8) * mm, "end": v(-12.69, -7) * mm});
            skLineSegment(sketch, "E327", {"start": v(-12.69, -7) * mm, "end": v(-12.14, -6.03) * mm});
            skLineSegment(sketch, "E328", {"start": v(-12.14, -6.03) * mm, "end": v(-11.62, -5.18) * mm});
            skLineSegment(sketch, "E329", {"start": v(-11.62, -5.18) * mm, "end": v(-11.13, -4.42) * mm});
            skLineSegment(sketch, "E330", {"start": v(-11.13, -4.42) * mm, "end": v(-10.65, -3.76) * mm});
            skLineSegment(sketch, "E331", {"start": v(-10.65, -3.76) * mm, "end": v(-10.2, -3.2) * mm});
            skLineSegment(sketch, "E332", {"start": v(-10.2, -3.2) * mm, "end": v(-9.77, -2.72) * mm});
            skLineSegment(sketch, "E333", {"start": v(-9.77, -2.72) * mm, "end": v(-9.47, -2.41) * mm});
            skLineSegment(sketch, "E334", {"start": v(-9.47, -2.41) * mm, "end": v(-9.36, -2.32) * mm});
            skLineSegment(sketch, "E335", {"start": v(-9.36, -2.32) * mm, "end": v(-9.19, -2.36) * mm});
            skLineSegment(sketch, "E336", {"start": v(-9.19, -2.36) * mm, "end": v(-8.7, -2.6) * mm});
            skLineSegment(sketch, "E337", {"start": v(-8.7, -2.6) * mm, "end": v(-8.2, -3.02) * mm});
            skLineSegment(sketch, "E338", {"start": v(-8.2, -3.02) * mm, "end": v(-7.83, -3.56) * mm});
            skLineSegment(sketch, "E339", {"start": v(-7.83, -3.56) * mm, "end": v(-7.59, -4.16) * mm});
            skLineSegment(sketch, "E340", {"start": v(-7.59, -4.16) * mm, "end": v(-7.43, -4.78) * mm});
            skLineSegment(sketch, "E341", {"start": v(-7.43, -4.78) * mm, "end": v(-7.35, -5.38) * mm});
            skLineSegment(sketch, "E342", {"start": v(-7.35, -5.38) * mm, "end": v(-7.33, -5.9) * mm});
            skLineSegment(sketch, "E343", {"start": v(-7.33, -5.9) * mm, "end": v(-7.34, -6.23) * mm});
            skLineSegment(sketch, "E344", {"start": v(-7.34, -6.23) * mm, "end": v(-7.34, -6.33) * mm});
            skLineSegment(sketch, "E345", {"start": v(-7.34, -6.33) * mm, "end": v(-7.36, -6.3) * mm});
            skLineSegment(sketch, "E346", {"start": v(-7.36, -6.3) * mm, "end": v(-7.41, -6.2) * mm});
            skLineSegment(sketch, "E347", {"start": v(-7.41, -6.2) * mm, "end": v(-7.5, -6.08) * mm});
            skLineSegment(sketch, "E348", {"start": v(-7.5, -6.08) * mm, "end": v(-7.6, -5.98) * mm});
            skLineSegment(sketch, "E349", {"start": v(-7.6, -5.98) * mm, "end": v(-7.67, -5.93) * mm});
            skLineSegment(sketch, "E350", {"start": v(-7.67, -5.93) * mm, "end": v(-7.7, -5.92) * mm});
            skLineSegment(sketch, "E351", {"start": v(-7.7, -5.92) * mm, "end": v(-7.74, -5.98) * mm});
            skLineSegment(sketch, "E352", {"start": v(-7.74, -5.98) * mm, "end": v(-7.78, -6.2) * mm});
            skLineSegment(sketch, "E353", {"start": v(-7.78, -6.2) * mm, "end": v(-7.82, -6.62) * mm});
            skLineSegment(sketch, "E354", {"start": v(-7.82, -6.62) * mm, "end": v(-7.88, -7.1) * mm});
            skLineSegment(sketch, "E355", {"start": v(-7.88, -7.1) * mm, "end": v(-8, -7.47) * mm});
            skLineSegment(sketch, "E356", {"start": v(-8, -7.47) * mm, "end": v(-8.05, -7.58) * mm});
            skLineSegment(sketch, "E357", {"start": v(-8.05, -7.58) * mm, "end": v(-8.06, -7.55) * mm});
            skLineSegment(sketch, "E358", {"start": v(-8.06, -7.55) * mm, "end": v(-8.09, -7.43) * mm});
            skLineSegment(sketch, "E359", {"start": v(-8.09, -7.43) * mm, "end": v(-8.14, -7.32) * mm});
            skLineSegment(sketch, "E360", {"start": v(-8.14, -7.32) * mm, "end": v(-8.2, -7.23) * mm});
            skLineSegment(sketch, "E361", {"start": v(-8.2, -7.23) * mm, "end": v(-8.28, -7.16) * mm});
            skLineSegment(sketch, "E362", {"start": v(-8.28, -7.16) * mm, "end": v(-8.3, -7.15) * mm});
            skLineSegment(sketch, "E363", {"start": v(-8.3, -7.15) * mm, "end": v(-8.34, -7.25) * mm});
            skLineSegment(sketch, "E364", {"start": v(-8.34, -7.25) * mm, "end": v(-8.44, -7.57) * mm});
            skLineSegment(sketch, "E365", {"start": v(-8.44, -7.57) * mm, "end": v(-8.58, -7.97) * mm});
            skLineSegment(sketch, "E366", {"start": v(-8.58, -7.97) * mm, "end": v(-8.74, -8.34) * mm});
            skLineSegment(sketch, "E367", {"start": v(-8.74, -8.34) * mm, "end": v(-8.87, -8.58) * mm});
            skLineSegment(sketch, "E368", {"start": v(-8.87, -8.58) * mm, "end": v(-8.93, -8.65) * mm});
            skLineSegment(sketch, "E369", {"start": v(-8.93, -8.65) * mm, "end": v(-8.93, -8.61) * mm});
            skLineSegment(sketch, "E370", {"start": v(-8.93, -8.61) * mm, "end": v(-8.93, -8.5) * mm});
            skLineSegment(sketch, "E371", {"start": v(-8.93, -8.5) * mm, "end": v(-8.93, -8.36) * mm});
            skLineSegment(sketch, "E372", {"start": v(-8.93, -8.36) * mm, "end": v(-8.97, -8.2) * mm});
            skLineSegment(sketch, "E373", {"start": v(-8.97, -8.2) * mm, "end": v(-9.03, -8.07) * mm});
            skLineSegment(sketch, "E374", {"start": v(-9.03, -8.07) * mm, "end": v(-9.06, -8.03) * mm});
            skLineSegment(sketch, "E375", {"start": v(-9.06, -8.03) * mm, "end": v(-9.13, -8.16) * mm});
            skLineSegment(sketch, "E376", {"start": v(-9.13, -8.16) * mm, "end": v(-9.45, -8.78) * mm});
            skLineSegment(sketch, "E377", {"start": v(-9.45, -8.78) * mm, "end": v(-9.84, -9.37) * mm});
            skLineSegment(sketch, "E378", {"start": v(-9.84, -9.37) * mm, "end": v(-9.95, -9.47) * mm});
            skLineSegment(sketch, "E379", {"start": v(-9.95, -9.47) * mm, "end": v(-9.95, -9.42) * mm});
            skLineSegment(sketch, "E380", {"start": v(-9.95, -9.42) * mm, "end": v(-9.95, -9.28) * mm});
            skLineSegment(sketch, "E381", {"start": v(-9.95, -9.28) * mm, "end": v(-9.96, -9.1) * mm});
            skLineSegment(sketch, "E382", {"start": v(-9.96, -9.1) * mm, "end": v(-9.99, -8.95) * mm});
            skLineSegment(sketch, "E383", {"start": v(-9.99, -8.95) * mm, "end": v(-10.02, -8.87) * mm});
            skLineSegment(sketch, "E384", {"start": v(-10.02, -8.87) * mm, "end": v(-10.04, -8.86) * mm});
            skLineSegment(sketch, "E385", {"start": v(-10.04, -8.86) * mm, "end": v(-10.11, -8.97) * mm});
            skLineSegment(sketch, "E386", {"start": v(-10.11, -8.97) * mm, "end": v(-10.49, -9.48) * mm});
            skLineSegment(sketch, "E387", {"start": v(-10.49, -9.48) * mm, "end": v(-10.9, -9.93) * mm});
            skLineSegment(sketch, "E388", {"start": v(-10.9, -9.93) * mm, "end": v(-10.98, -10.01) * mm});
            skLineSegment(sketch, "E389", {"start": v(-10.98, -10.01) * mm, "end": v(-10.97, -9.95) * mm});
            skLineSegment(sketch, "E390", {"start": v(-10.97, -9.95) * mm, "end": v(-10.96, -9.78) * mm});
            skLineSegment(sketch, "E391", {"start": v(-10.96, -9.78) * mm, "end": v(-10.97, -9.6) * mm});
            skLineSegment(sketch, "E392", {"start": v(-10.97, -9.6) * mm, "end": v(-11, -9.5) * mm});
            skLineSegment(sketch, "E393", {"start": v(-11, -9.5) * mm, "end": v(-11.02, -9.43) * mm});
            skLineSegment(sketch, "E394", {"start": v(-11.02, -9.43) * mm, "end": v(-11.04, -9.41) * mm});
            skLineSegment(sketch, "E395", {"start": v(-11.04, -9.41) * mm, "end": v(-11.1, -9.48) * mm});
            skLineSegment(sketch, "E396", {"start": v(-11.1, -9.48) * mm, "end": v(-11.3, -9.68) * mm});
            skLineSegment(sketch, "E397", {"start": v(-11.3, -9.68) * mm, "end": v(-11.55, -9.96) * mm});
            skLineSegment(sketch, "E398", {"start": v(-11.55, -9.96) * mm, "end": v(-11.81, -10.2) * mm});
            skLineSegment(sketch, "E399", {"start": v(-11.81, -10.2) * mm, "end": v(-12.04, -10.36) * mm});
            skLineSegment(sketch, "E400", {"start": v(-12.04, -10.36) * mm, "end": v(-12.12, -10.4) * mm});
            skLineSegment(sketch, "E401", {"start": v(-12.12, -10.4) * mm, "end": v(-12.1, -10.35) * mm});
            skLineSegment(sketch, "E402", {"start": v(-12.1, -10.35) * mm, "end": v(-12.06, -10.2) * mm});
            skLineSegment(sketch, "E403", {"start": v(-12.06, -10.2) * mm, "end": v(-12.04, -10.02) * mm});
            skLineSegment(sketch, "E404", {"start": v(-12.04, -10.02) * mm, "end": v(-12.05, -9.86) * mm});
            skLineSegment(sketch, "E405", {"start": v(-12.05, -9.86) * mm, "end": v(-12.1, -9.74) * mm});
            skLineSegment(sketch, "E406", {"start": v(-12.1, -9.74) * mm, "end": v(-12.12, -9.71) * mm});
            skLineSegment(sketch, "E407", {"start": v(-12.12, -9.71) * mm, "end": v(-12.18, -9.73) * mm});
            skLineSegment(sketch, "E408", {"start": v(-12.18, -9.73) * mm, "end": v(-12.31, -9.86) * mm});
            skLineSegment(sketch, "E409", {"start": v(-12.31, -9.86) * mm, "end": v(-12.5, -10.1) * mm});
            skLineSegment(sketch, "E410", {"start": v(-12.5, -10.1) * mm, "end": v(-12.77, -10.37) * mm});
            skLineSegment(sketch, "E411", {"start": v(-12.77, -10.37) * mm, "end": v(-13.05, -10.57) * mm});
            skLineSegment(sketch, "E412", {"start": v(-13.05, -10.57) * mm, "end": v(-13.16, -10.61) * mm});
            skLineSegment(sketch, "E413", {"start": v(-13.16, -10.61) * mm, "end": v(-13.15, -10.56) * mm});
            skLineSegment(sketch, "E414", {"start": v(-13.15, -10.56) * mm, "end": v(-13.14, -10.4) * mm});
            skLineSegment(sketch, "E415", {"start": v(-13.14, -10.4) * mm, "end": v(-13.12, -10.21) * mm});
            skLineSegment(sketch, "E416", {"start": v(-13.12, -10.21) * mm, "end": v(-13.13, -10.06) * mm});
            skLineSegment(sketch, "E417", {"start": v(-13.13, -10.06) * mm, "end": v(-13.14, -10) * mm});
            skLineSegment(sketch, "E418", {"start": v(-13.14, -10) * mm, "end": v(-13.16, -9.98) * mm});
            skLineSegment(sketch, "E419", {"start": v(-13.16, -9.98) * mm, "end": v(-13.25, -10) * mm});
            skLineSegment(sketch, "E420", {"start": v(-13.25, -10) * mm, "end": v(-13.51, -10.1) * mm});
            skLineSegment(sketch, "E421", {"start": v(-13.51, -10.1) * mm, "end": v(-13.8, -10.23) * mm});
            skLineSegment(sketch, "E422", {"start": v(-13.8, -10.23) * mm, "end": v(-14.06, -10.39) * mm});
            skLineSegment(sketch, "E423", {"start": v(-14.06, -10.39) * mm, "end": v(-14.24, -10.5) * mm});
            skLineSegment(sketch, "E424", {"start": v(-14.24, -10.5) * mm, "end": v(-14.3, -10.55) * mm});
            skLineSegment(sketch, "E425", {"start": v(-14.3, -10.55) * mm, "end": v(-14.3, -10.43) * mm});
            skLineSegment(sketch, "E426", {"start": v(-14.3, -10.43) * mm, "end": v(-14.3, -10.06) * mm});
            skLineSegment(sketch, "E427", {"start": v(-14.3, -10.06) * mm, "end": v(-14.3, -9.58) * mm});
            skLineSegment(sketch, "E428", {"start": v(-14.3, -9.58) * mm, "end": v(-14.31, -9.2) * mm});
            skLineSegment(sketch, "E429", {"start": v(-14.31, -9.2) * mm, "end": v(-14.34, -9.08) * mm});
            skLineSegment(sketch, "E430", {"start": v(-14.34, -9.08) * mm, "end": v(-14.72, -9.45) * mm});
            skLineSegment(sketch, "E431", {"start": v(-14.72, -9.45) * mm, "end": v(-14.75, -9.35) * mm});
            skLineSegment(sketch, "E432", {"start": v(-14.75, -9.35) * mm, "end": v(-14.78, -9.01) * mm});
            skLineSegment(sketch, "E433", {"start": v(-14.78, -9.01) * mm, "end": v(-14.75, -8.59) * mm});
            skLineSegment(sketch, "E434", {"start": v(-14.75, -8.59) * mm, "end": v(-14.66, -8.19) * mm});
            skLineSegment(sketch, "E435", {"start": v(-14.66, -8.19) * mm, "end": v(-14.59, -7.92) * mm});
            skLineSegment(sketch, "E436", {"start": v(-14.59, -7.92) * mm, "end": v(-14.56, -7.83) * mm});
            skLineSegment(sketch, "E437", {"start": v(-14.56, -7.83) * mm, "end": v(-14.58, -7.8) * mm});
            skLineSegment(sketch, "E438", {"start": v(-14.58, -7.8) * mm, "end": v(-14.68, -7.75) * mm});
            skLineSegment(sketch, "E439", {"start": v(-14.68, -7.75) * mm, "end": v(-14.82, -7.8) * mm});
            skLineSegment(sketch, "E440", {"start": v(-14.82, -7.8) * mm, "end": v(-14.96, -7.9) * mm});
            skLineSegment(sketch, "E441", {"start": v(-14.96, -7.9) * mm, "end": v(-15.07, -8.03) * mm});
            skLineSegment(sketch, "E442", {"start": v(-15.07, -8.03) * mm, "end": v(-15.1, -8.07) * mm});
            skLineSegment(sketch, "E443", {"start": v(-15.1, -8.07) * mm, "end": v(-15.1, -7.95) * mm});
            skLineSegment(sketch, "E444", {"start": v(-15.1, -7.95) * mm, "end": v(-14.97, -7.36) * mm});
            skLineSegment(sketch, "E445", {"start": v(-14.97, -7.36) * mm, "end": v(-14.8, -6.82) * mm});
            skLineSegment(sketch, "E446", {"start": v(-14.8, -6.82) * mm, "end": v(-14.77, -6.72) * mm});
            skLineSegment(sketch, "E447", {"start": v(-14.77, -6.72) * mm, "end": v(-14.8, -6.7) * mm});
            skLineSegment(sketch, "E448", {"start": v(-14.8, -6.7) * mm, "end": v(-14.92, -6.65) * mm});
            skLineSegment(sketch, "E449", {"start": v(-14.92, -6.65) * mm, "end": v(-15.06, -6.73) * mm});
            skLineSegment(sketch, "E450", {"start": v(-15.06, -6.73) * mm, "end": v(-15.21, -6.88) * mm});
            skLineSegment(sketch, "E451", {"start": v(-15.21, -6.88) * mm, "end": v(-15.32, -7) * mm});
            skLineSegment(sketch, "E452", {"start": v(-15.32, -7) * mm, "end": v(-15.36, -7.03) * mm});
            skLineSegment(sketch, "E453", {"start": v(-15.36, -7.03) * mm, "end": v(-15.33, -6.9) * mm});
            skLineSegment(sketch, "E454", {"start": v(-15.33, -6.9) * mm, "end": v(-15.24, -6.53) * mm});
            skLineSegment(sketch, "E455", {"start": v(-15.24, -6.53) * mm, "end": v(-15.1, -6.16) * mm});
            skLineSegment(sketch, "E456", {"start": v(-15.1, -6.16) * mm, "end": v(-14.95, -5.86) * mm});
            skLineSegment(sketch, "E457", {"start": v(-14.95, -5.86) * mm, "end": v(-14.84, -5.68) * mm});
            skLineSegment(sketch, "E458", {"start": v(-14.84, -5.68) * mm, "end": v(-14.8, -5.61) * mm});
            skLineSegment(sketch, "E459", {"start": v(-14.8, -5.61) * mm, "end": v(-14.83, -5.58) * mm});
            skLineSegment(sketch, "E460", {"start": v(-14.83, -5.58) * mm, "end": v(-14.96, -5.52) * mm});
            skLineSegment(sketch, "E461", {"start": v(-14.96, -5.52) * mm, "end": v(-15.12, -5.54) * mm});
            skLineSegment(sketch, "E462", {"start": v(-15.12, -5.54) * mm, "end": v(-15.27, -5.64) * mm});
            skLineSegment(sketch, "E463", {"start": v(-15.27, -5.64) * mm, "end": v(-15.38, -5.73) * mm});
            skLineSegment(sketch, "E464", {"start": v(-15.38, -5.73) * mm, "end": v(-15.41, -5.76) * mm});
            skLineSegment(sketch, "E465", {"start": v(-15.41, -5.76) * mm, "end": v(-15.38, -5.66) * mm});
            skLineSegment(sketch, "E466", {"start": v(-15.38, -5.66) * mm, "end": v(-15.24, -5.37) * mm});
            skLineSegment(sketch, "E467", {"start": v(-15.24, -5.37) * mm, "end": v(-15.05, -5.06) * mm});
            skLineSegment(sketch, "E468", {"start": v(-15.05, -5.06) * mm, "end": v(-14.85, -4.8) * mm});
            skLineSegment(sketch, "E469", {"start": v(-14.85, -4.8) * mm, "end": v(-14.7, -4.63) * mm});
            skLineSegment(sketch, "E470", {"start": v(-14.7, -4.63) * mm, "end": v(-14.65, -4.57) * mm});
            skLineSegment(sketch, "E471", {"start": v(-14.65, -4.57) * mm, "end": v(-14.68, -4.55) * mm});
            skLineSegment(sketch, "E472", {"start": v(-14.68, -4.55) * mm, "end": v(-14.75, -4.48) * mm});
            skLineSegment(sketch, "E473", {"start": v(-14.75, -4.48) * mm, "end": v(-14.87, -4.42) * mm});
            skLineSegment(sketch, "E474", {"start": v(-14.87, -4.42) * mm, "end": v(-15.03, -4.4) * mm});
            skLineSegment(sketch, "E475", {"start": v(-15.03, -4.4) * mm, "end": v(-15.2, -4.46) * mm});
            skLineSegment(sketch, "E476", {"start": v(-15.2, -4.46) * mm, "end": v(-15.24, -4.5) * mm});
            skLineSegment(sketch, "E477", {"start": v(-15.24, -4.5) * mm, "end": v(-15.19, -4.4) * mm});
            skLineSegment(sketch, "E478", {"start": v(-15.19, -4.4) * mm, "end": v(-14.86, -3.95) * mm});
            skLineSegment(sketch, "E479", {"start": v(-14.86, -3.95) * mm, "end": v(-14.5, -3.6) * mm});
            skLineSegment(sketch, "E480", {"start": v(-14.5, -3.6) * mm, "end": v(-14.41, -3.54) * mm});
            skLineSegment(sketch, "E481", {"start": v(-14.41, -3.54) * mm, "end": v(-14.44, -3.5) * mm});
            skLineSegment(sketch, "E482", {"start": v(-14.44, -3.5) * mm, "end": v(-14.55, -3.41) * mm});
            skLineSegment(sketch, "E483", {"start": v(-14.55, -3.41) * mm, "end": v(-14.7, -3.37) * mm});
            skLineSegment(sketch, "E484", {"start": v(-14.7, -3.37) * mm, "end": v(-14.85, -3.38) * mm});
            skLineSegment(sketch, "E485", {"start": v(-14.85, -3.38) * mm, "end": v(-14.96, -3.39) * mm});
            skLineSegment(sketch, "E486", {"start": v(-14.96, -3.39) * mm, "end": v(-15, -3.39) * mm});
            skLineSegment(sketch, "E487", {"start": v(-15, -3.39) * mm, "end": v(-14.92, -3.28) * mm});
            skLineSegment(sketch, "E488", {"start": v(-14.92, -3.28) * mm, "end": v(-14.47, -2.84) * mm});
            skLineSegment(sketch, "E489", {"start": v(-14.47, -2.84) * mm, "end": v(-14.01, -2.44) * mm});
            skLineSegment(sketch, "E490", {"start": v(-14.01, -2.44) * mm, "end": v(-13.92, -2.36) * mm});
            skLineSegment(sketch, "E491", {"start": v(-13.92, -2.36) * mm, "end": v(-13.93, -2.34) * mm});
            skLineSegment(sketch, "E492", {"start": v(-13.93, -2.34) * mm, "end": v(-14.08, -2.26) * mm});
            skLineSegment(sketch, "E493", {"start": v(-14.08, -2.26) * mm, "end": v(-14.33, -2.2) * mm});
            skLineSegment(sketch, "E494", {"start": v(-14.33, -2.2) * mm, "end": v(-14.4, -2.18) * mm});
            skLineSegment(sketch, "E495", {"start": v(-14.4, -2.18) * mm, "end": v(-14.3, -2.07) * mm});
            skLineSegment(sketch, "E496", {"start": v(-14.3, -2.07) * mm, "end": v(-13.96, -1.78) * mm});
            skLineSegment(sketch, "E497", {"start": v(-13.96, -1.78) * mm, "end": v(-13.42, -1.4) * mm});
            skLineSegment(sketch, "E498", {"start": v(-13.42, -1.4) * mm, "end": v(-12.8, -1.06) * mm});
            skLineSegment(sketch, "E499", {"start": v(-12.8, -1.06) * mm, "end": v(-12.16, -0.83) * mm});
            skLineSegment(sketch, "E500", {"start": v(-12.16, -0.83) * mm, "end": v(-11.51, -0.74) * mm});
            skLineSegment(sketch, "E501", {"start": v(-11.51, -0.74) * mm, "end": v(-10.9, -0.84) * mm});
            skLineSegment(sketch, "E502", {"start": v(-10.9, -0.84) * mm, "end": v(-10.36, -1.18) * mm});
            skLineSegment(sketch, "E503", {"start": v(-10.36, -1.18) * mm, "end": v(-10, -1.64) * mm});
            skLineSegment(sketch, "E504", {"start": v(-10, -1.64) * mm, "end": v(-9.92, -1.8) * mm});
            skLineSegment(sketch, "E505", {"start": v(-9.92, -1.8) * mm, "end": v(-10.2, -2.14) * mm});
            skLineSegment(sketch, "E506", {"start": v(-10.2, -2.14) * mm, "end": v(-10.95, -3.2) * mm});
            skLineSegment(sketch, "E507", {"start": v(-10.95, -3.2) * mm, "end": v(-11.84, -4.73) * mm});
            skLineSegment(sketch, "E508", {"start": v(-11.84, -4.73) * mm, "end": v(-12.6, -6.35) * mm});
            skLineSegment(sketch, "E509", {"start": v(-12.6, -6.35) * mm, "end": v(-13.11, -7.64) * mm});
            skLineSegment(sketch, "E510", {"start": v(-13.11, -7.64) * mm, "end": v(-13.26, -8.07) * mm});
            skLineSegment(sketch, "E511", {"start": v(-13.26, 8) * mm, "end": v(-13.12, 7.74) * mm});
            skLineSegment(sketch, "E512", {"start": v(-13.12, 7.74) * mm, "end": v(-12.69, 6.93) * mm});
            skLineSegment(sketch, "E513", {"start": v(-12.69, 6.93) * mm, "end": v(-12.14, 5.97) * mm});
            skLineSegment(sketch, "E514", {"start": v(-12.14, 5.97) * mm, "end": v(-11.62, 5.1) * mm});
            skLineSegment(sketch, "E515", {"start": v(-11.62, 5.1) * mm, "end": v(-11.13, 4.35) * mm});
            skLineSegment(sketch, "E516", {"start": v(-11.13, 4.35) * mm, "end": v(-10.65, 3.7) * mm});
            skLineSegment(sketch, "E517", {"start": v(-10.65, 3.7) * mm, "end": v(-10.2, 3.13) * mm});
            skLineSegment(sketch, "E518", {"start": v(-10.2, 3.13) * mm, "end": v(-9.77, 2.65) * mm});
            skLineSegment(sketch, "E519", {"start": v(-9.77, 2.65) * mm, "end": v(-9.47, 2.35) * mm});
            skLineSegment(sketch, "E520", {"start": v(-9.47, 2.35) * mm, "end": v(-9.36, 2.25) * mm});
            skLineSegment(sketch, "E521", {"start": v(-9.36, 2.25) * mm, "end": v(-9.19, 2.3) * mm});
            skLineSegment(sketch, "E522", {"start": v(-9.19, 2.3) * mm, "end": v(-8.7, 2.53) * mm});
            skLineSegment(sketch, "E523", {"start": v(-8.7, 2.53) * mm, "end": v(-8.2, 2.95) * mm});
            skLineSegment(sketch, "E524", {"start": v(-8.2, 2.95) * mm, "end": v(-7.83, 3.49) * mm});
            skLineSegment(sketch, "E525", {"start": v(-7.83, 3.49) * mm, "end": v(-7.59, 4.09) * mm});
            skLineSegment(sketch, "E526", {"start": v(-7.59, 4.09) * mm, "end": v(-7.43, 4.71) * mm});
            skLineSegment(sketch, "E527", {"start": v(-7.43, 4.71) * mm, "end": v(-7.35, 5.3) * mm});
            skLineSegment(sketch, "E528", {"start": v(-7.35, 5.3) * mm, "end": v(-7.33, 5.84) * mm});
            skLineSegment(sketch, "E529", {"start": v(-7.33, 5.84) * mm, "end": v(-7.34, 6.16) * mm});
            skLineSegment(sketch, "E530", {"start": v(-7.34, 6.16) * mm, "end": v(-7.34, 6.27) * mm});
            skLineSegment(sketch, "E531", {"start": v(-7.34, 6.27) * mm, "end": v(-7.36, 6.23) * mm});
            skLineSegment(sketch, "E532", {"start": v(-7.36, 6.23) * mm, "end": v(-7.41, 6.13) * mm});
            skLineSegment(sketch, "E533", {"start": v(-7.41, 6.13) * mm, "end": v(-7.5, 6) * mm});
            skLineSegment(sketch, "E534", {"start": v(-7.5, 6) * mm, "end": v(-7.6, 5.92) * mm});
            skLineSegment(sketch, "E535", {"start": v(-7.6, 5.92) * mm, "end": v(-7.67, 5.86) * mm});
            skLineSegment(sketch, "E536", {"start": v(-7.67, 5.86) * mm, "end": v(-7.7, 5.85) * mm});
            skLineSegment(sketch, "E537", {"start": v(-7.7, 5.85) * mm, "end": v(-7.74, 5.9) * mm});
            skLineSegment(sketch, "E538", {"start": v(-7.74, 5.9) * mm, "end": v(-7.78, 6.13) * mm});
            skLineSegment(sketch, "E539", {"start": v(-7.78, 6.13) * mm, "end": v(-7.82, 6.55) * mm});
            skLineSegment(sketch, "E540", {"start": v(-7.82, 6.55) * mm, "end": v(-7.88, 7.04) * mm});
            skLineSegment(sketch, "E541", {"start": v(-7.88, 7.04) * mm, "end": v(-8, 7.4) * mm});
            skLineSegment(sketch, "E542", {"start": v(-8, 7.4) * mm, "end": v(-8.05, 7.52) * mm});
            skLineSegment(sketch, "E543", {"start": v(-8.05, 7.52) * mm, "end": v(-8.06, 7.48) * mm});
            skLineSegment(sketch, "E544", {"start": v(-8.06, 7.48) * mm, "end": v(-8.09, 7.37) * mm});
            skLineSegment(sketch, "E545", {"start": v(-8.09, 7.37) * mm, "end": v(-8.14, 7.25) * mm});
            skLineSegment(sketch, "E546", {"start": v(-8.14, 7.25) * mm, "end": v(-8.2, 7.16) * mm});
            skLineSegment(sketch, "E547", {"start": v(-8.2, 7.16) * mm, "end": v(-8.28, 7.1) * mm});
            skLineSegment(sketch, "E548", {"start": v(-8.28, 7.1) * mm, "end": v(-8.3, 7.08) * mm});
            skLineSegment(sketch, "E549", {"start": v(-8.3, 7.08) * mm, "end": v(-8.34, 7.18) * mm});
            skLineSegment(sketch, "E550", {"start": v(-8.34, 7.18) * mm, "end": v(-8.44, 7.5) * mm});
            skLineSegment(sketch, "E551", {"start": v(-8.44, 7.5) * mm, "end": v(-8.58, 7.9) * mm});
            skLineSegment(sketch, "E552", {"start": v(-8.58, 7.9) * mm, "end": v(-8.74, 8.28) * mm});
            skLineSegment(sketch, "E553", {"start": v(-8.74, 8.28) * mm, "end": v(-8.87, 8.51) * mm});
            skLineSegment(sketch, "E554", {"start": v(-8.87, 8.51) * mm, "end": v(-8.93, 8.58) * mm});
            skLineSegment(sketch, "E555", {"start": v(-8.93, 8.58) * mm, "end": v(-8.93, 8.55) * mm});
            skLineSegment(sketch, "E556", {"start": v(-8.93, 8.55) * mm, "end": v(-8.93, 8.44) * mm});
            skLineSegment(sketch, "E557", {"start": v(-8.93, 8.44) * mm, "end": v(-8.93, 8.3) * mm});
            skLineSegment(sketch, "E558", {"start": v(-8.93, 8.3) * mm, "end": v(-8.97, 8.14) * mm});
            skLineSegment(sketch, "E559", {"start": v(-8.97, 8.14) * mm, "end": v(-9.03, 8) * mm});
            skLineSegment(sketch, "E560", {"start": v(-9.03, 8) * mm, "end": v(-9.06, 7.97) * mm});
            skLineSegment(sketch, "E561", {"start": v(-9.06, 7.97) * mm, "end": v(-9.13, 8.1) * mm});
            skLineSegment(sketch, "E562", {"start": v(-9.13, 8.1) * mm, "end": v(-9.45, 8.72) * mm});
            skLineSegment(sketch, "E563", {"start": v(-9.45, 8.72) * mm, "end": v(-9.84, 9.3) * mm});
            skLineSegment(sketch, "E564", {"start": v(-9.84, 9.3) * mm, "end": v(-9.95, 9.4) * mm});
            skLineSegment(sketch, "E565", {"start": v(-9.95, 9.4) * mm, "end": v(-9.95, 9.35) * mm});
            skLineSegment(sketch, "E566", {"start": v(-9.95, 9.35) * mm, "end": v(-9.95, 9.21) * mm});
            skLineSegment(sketch, "E567", {"start": v(-9.95, 9.21) * mm, "end": v(-9.96, 9.03) * mm});
            skLineSegment(sketch, "E568", {"start": v(-9.96, 9.03) * mm, "end": v(-9.99, 8.88) * mm});
            skLineSegment(sketch, "E569", {"start": v(-9.99, 8.88) * mm, "end": v(-10.02, 8.8) * mm});
            skLineSegment(sketch, "E570", {"start": v(-10.02, 8.8) * mm, "end": v(-10.04, 8.8) * mm});
            skLineSegment(sketch, "E571", {"start": v(-10.04, 8.8) * mm, "end": v(-10.11, 8.9) * mm});
            skLineSegment(sketch, "E572", {"start": v(-10.11, 8.9) * mm, "end": v(-10.49, 9.42) * mm});
            skLineSegment(sketch, "E573", {"start": v(-10.49, 9.42) * mm, "end": v(-10.9, 9.86) * mm});
            skLineSegment(sketch, "E574", {"start": v(-10.9, 9.86) * mm, "end": v(-10.98, 9.94) * mm});
            skLineSegment(sketch, "E575", {"start": v(-10.98, 9.94) * mm, "end": v(-10.97, 9.89) * mm});
            skLineSegment(sketch, "E576", {"start": v(-10.97, 9.89) * mm, "end": v(-10.96, 9.71) * mm});
            skLineSegment(sketch, "E577", {"start": v(-10.96, 9.71) * mm, "end": v(-10.97, 9.54) * mm});
            skLineSegment(sketch, "E578", {"start": v(-10.97, 9.54) * mm, "end": v(-11, 9.43) * mm});
            skLineSegment(sketch, "E579", {"start": v(-11, 9.43) * mm, "end": v(-11.02, 9.36) * mm});
            skLineSegment(sketch, "E580", {"start": v(-11.02, 9.36) * mm, "end": v(-11.04, 9.35) * mm});
            skLineSegment(sketch, "E581", {"start": v(-11.04, 9.35) * mm, "end": v(-11.1, 9.41) * mm});
            skLineSegment(sketch, "E582", {"start": v(-11.1, 9.41) * mm, "end": v(-11.3, 9.62) * mm});
            skLineSegment(sketch, "E583", {"start": v(-11.3, 9.62) * mm, "end": v(-11.55, 9.89) * mm});
            skLineSegment(sketch, "E584", {"start": v(-11.55, 9.89) * mm, "end": v(-11.81, 10.14) * mm});
            skLineSegment(sketch, "E585", {"start": v(-11.81, 10.14) * mm, "end": v(-12.04, 10.3) * mm});
            skLineSegment(sketch, "E586", {"start": v(-12.04, 10.3) * mm, "end": v(-12.12, 10.33) * mm});
            skLineSegment(sketch, "E587", {"start": v(-12.12, 10.33) * mm, "end": v(-12.1, 10.28) * mm});
            skLineSegment(sketch, "E588", {"start": v(-12.1, 10.28) * mm, "end": v(-12.06, 10.14) * mm});
            skLineSegment(sketch, "E589", {"start": v(-12.06, 10.14) * mm, "end": v(-12.04, 9.95) * mm});
            skLineSegment(sketch, "E590", {"start": v(-12.04, 9.95) * mm, "end": v(-12.05, 9.79) * mm});
            skLineSegment(sketch, "E591", {"start": v(-12.05, 9.79) * mm, "end": v(-12.1, 9.68) * mm});
            skLineSegment(sketch, "E592", {"start": v(-12.1, 9.68) * mm, "end": v(-12.12, 9.65) * mm});
            skLineSegment(sketch, "E593", {"start": v(-12.12, 9.65) * mm, "end": v(-12.18, 9.67) * mm});
            skLineSegment(sketch, "E594", {"start": v(-12.18, 9.67) * mm, "end": v(-12.31, 9.8) * mm});
            skLineSegment(sketch, "E595", {"start": v(-12.31, 9.8) * mm, "end": v(-12.5, 10.03) * mm});
            skLineSegment(sketch, "E596", {"start": v(-12.5, 10.03) * mm, "end": v(-12.77, 10.3) * mm});
            skLineSegment(sketch, "E597", {"start": v(-12.77, 10.3) * mm, "end": v(-13.05, 10.5) * mm});
            skLineSegment(sketch, "E598", {"start": v(-13.05, 10.5) * mm, "end": v(-13.16, 10.55) * mm});
            skLineSegment(sketch, "E599", {"start": v(-13.16, 10.55) * mm, "end": v(-13.15, 10.5) * mm});
            skLineSegment(sketch, "E600", {"start": v(-13.15, 10.5) * mm, "end": v(-13.14, 10.34) * mm});
            skLineSegment(sketch, "E601", {"start": v(-13.14, 10.34) * mm, "end": v(-13.12, 10.15) * mm});
            skLineSegment(sketch, "E602", {"start": v(-13.12, 10.15) * mm, "end": v(-13.13, 10) * mm});
            skLineSegment(sketch, "E603", {"start": v(-13.13, 10) * mm, "end": v(-13.14, 9.93) * mm});
            skLineSegment(sketch, "E604", {"start": v(-13.14, 9.93) * mm, "end": v(-13.16, 9.91) * mm});
            skLineSegment(sketch, "E605", {"start": v(-13.16, 9.91) * mm, "end": v(-13.25, 9.93) * mm});
            skLineSegment(sketch, "E606", {"start": v(-13.25, 9.93) * mm, "end": v(-13.51, 10.02) * mm});
            skLineSegment(sketch, "E607", {"start": v(-13.51, 10.02) * mm, "end": v(-13.8, 10.16) * mm});
            skLineSegment(sketch, "E608", {"start": v(-13.8, 10.16) * mm, "end": v(-14.06, 10.32) * mm});
            skLineSegment(sketch, "E609", {"start": v(-14.06, 10.32) * mm, "end": v(-14.24, 10.44) * mm});
            skLineSegment(sketch, "E610", {"start": v(-14.24, 10.44) * mm, "end": v(-14.3, 10.48) * mm});
            skLineSegment(sketch, "E611", {"start": v(-14.3, 10.48) * mm, "end": v(-14.3, 10.36) * mm});
            skLineSegment(sketch, "E612", {"start": v(-14.3, 10.36) * mm, "end": v(-14.3, 10) * mm});
            skLineSegment(sketch, "E613", {"start": v(-14.3, 10) * mm, "end": v(-14.3, 9.5) * mm});
            skLineSegment(sketch, "E614", {"start": v(-14.3, 9.5) * mm, "end": v(-14.31, 9.14) * mm});
            skLineSegment(sketch, "E615", {"start": v(-14.31, 9.14) * mm, "end": v(-14.34, 9.02) * mm});
            skLineSegment(sketch, "E616", {"start": v(-14.34, 9.02) * mm, "end": v(-14.72, 9.39) * mm});
            skLineSegment(sketch, "E617", {"start": v(-14.72, 9.39) * mm, "end": v(-14.75, 9.28) * mm});
            skLineSegment(sketch, "E618", {"start": v(-14.75, 9.28) * mm, "end": v(-14.78, 8.95) * mm});
            skLineSegment(sketch, "E619", {"start": v(-14.78, 8.95) * mm, "end": v(-14.75, 8.52) * mm});
            skLineSegment(sketch, "E620", {"start": v(-14.75, 8.52) * mm, "end": v(-14.66, 8.12) * mm});
            skLineSegment(sketch, "E621", {"start": v(-14.66, 8.12) * mm, "end": v(-14.59, 7.85) * mm});
            skLineSegment(sketch, "E622", {"start": v(-14.59, 7.85) * mm, "end": v(-14.56, 7.77) * mm});
            skLineSegment(sketch, "E623", {"start": v(-14.56, 7.77) * mm, "end": v(-14.58, 7.74) * mm});
            skLineSegment(sketch, "E624", {"start": v(-14.58, 7.74) * mm, "end": v(-14.68, 7.69) * mm});
            skLineSegment(sketch, "E625", {"start": v(-14.68, 7.69) * mm, "end": v(-14.82, 7.72) * mm});
            skLineSegment(sketch, "E626", {"start": v(-14.82, 7.72) * mm, "end": v(-14.96, 7.84) * mm});
            skLineSegment(sketch, "E627", {"start": v(-14.96, 7.84) * mm, "end": v(-15.07, 7.97) * mm});
            skLineSegment(sketch, "E628", {"start": v(-15.07, 7.97) * mm, "end": v(-15.1, 8) * mm});
            skLineSegment(sketch, "E629", {"start": v(-15.1, 8) * mm, "end": v(-15.1, 7.88) * mm});
            skLineSegment(sketch, "E630", {"start": v(-15.1, 7.88) * mm, "end": v(-14.97, 7.3) * mm});
            skLineSegment(sketch, "E631", {"start": v(-14.97, 7.3) * mm, "end": v(-14.8, 6.75) * mm});
            skLineSegment(sketch, "E632", {"start": v(-14.8, 6.75) * mm, "end": v(-14.77, 6.65) * mm});
            skLineSegment(sketch, "E633", {"start": v(-14.77, 6.65) * mm, "end": v(-14.8, 6.63) * mm});
            skLineSegment(sketch, "E634", {"start": v(-14.8, 6.63) * mm, "end": v(-14.92, 6.59) * mm});
            skLineSegment(sketch, "E635", {"start": v(-14.92, 6.59) * mm, "end": v(-15.06, 6.66) * mm});
            skLineSegment(sketch, "E636", {"start": v(-15.06, 6.66) * mm, "end": v(-15.21, 6.81) * mm});
            skLineSegment(sketch, "E637", {"start": v(-15.21, 6.81) * mm, "end": v(-15.32, 6.93) * mm});
            skLineSegment(sketch, "E638", {"start": v(-15.32, 6.93) * mm, "end": v(-15.36, 6.97) * mm});
            skLineSegment(sketch, "E639", {"start": v(-15.36, 6.97) * mm, "end": v(-15.33, 6.84) * mm});
            skLineSegment(sketch, "E640", {"start": v(-15.33, 6.84) * mm, "end": v(-15.24, 6.47) * mm});
            skLineSegment(sketch, "E641", {"start": v(-15.24, 6.47) * mm, "end": v(-15.1, 6.1) * mm});
            skLineSegment(sketch, "E642", {"start": v(-15.1, 6.1) * mm, "end": v(-14.95, 5.8) * mm});
            skLineSegment(sketch, "E643", {"start": v(-14.95, 5.8) * mm, "end": v(-14.84, 5.61) * mm});
            skLineSegment(sketch, "E644", {"start": v(-14.84, 5.61) * mm, "end": v(-14.8, 5.55) * mm});
            skLineSegment(sketch, "E645", {"start": v(-14.8, 5.55) * mm, "end": v(-14.83, 5.51) * mm});
            skLineSegment(sketch, "E646", {"start": v(-14.83, 5.51) * mm, "end": v(-14.97, 5.45) * mm});
            skLineSegment(sketch, "E647", {"start": v(-14.97, 5.45) * mm, "end": v(-15.12, 5.47) * mm});
            skLineSegment(sketch, "E648", {"start": v(-15.12, 5.47) * mm, "end": v(-15.27, 5.57) * mm});
            skLineSegment(sketch, "E649", {"start": v(-15.27, 5.57) * mm, "end": v(-15.38, 5.66) * mm});
            skLineSegment(sketch, "E650", {"start": v(-15.38, 5.66) * mm, "end": v(-15.41, 5.7) * mm});
            skLineSegment(sketch, "E651", {"start": v(-15.41, 5.7) * mm, "end": v(-15.38, 5.6) * mm});
            skLineSegment(sketch, "E652", {"start": v(-15.38, 5.6) * mm, "end": v(-15.24, 5.3) * mm});
            skLineSegment(sketch, "E653", {"start": v(-15.24, 5.3) * mm, "end": v(-15.05, 5) * mm});
            skLineSegment(sketch, "E654", {"start": v(-15.05, 5) * mm, "end": v(-14.85, 4.74) * mm});
            skLineSegment(sketch, "E655", {"start": v(-14.85, 4.74) * mm, "end": v(-14.7, 4.56) * mm});
            skLineSegment(sketch, "E656", {"start": v(-14.7, 4.56) * mm, "end": v(-14.65, 4.5) * mm});
            skLineSegment(sketch, "E657", {"start": v(-14.65, 4.5) * mm, "end": v(-14.68, 4.48) * mm});
            skLineSegment(sketch, "E658", {"start": v(-14.68, 4.48) * mm, "end": v(-14.75, 4.42) * mm});
            skLineSegment(sketch, "E659", {"start": v(-14.75, 4.42) * mm, "end": v(-14.87, 4.35) * mm});
            skLineSegment(sketch, "E660", {"start": v(-14.87, 4.35) * mm, "end": v(-15.03, 4.34) * mm});
            skLineSegment(sketch, "E661", {"start": v(-15.03, 4.34) * mm, "end": v(-15.2, 4.4) * mm});
            skLineSegment(sketch, "E662", {"start": v(-15.2, 4.4) * mm, "end": v(-15.25, 4.43) * mm});
            skLineSegment(sketch, "E663", {"start": v(-15.25, 4.43) * mm, "end": v(-15.19, 4.32) * mm});
            skLineSegment(sketch, "E664", {"start": v(-15.19, 4.32) * mm, "end": v(-14.86, 3.88) * mm});
            skLineSegment(sketch, "E665", {"start": v(-14.86, 3.88) * mm, "end": v(-14.5, 3.53) * mm});
            skLineSegment(sketch, "E666", {"start": v(-14.5, 3.53) * mm, "end": v(-14.41, 3.48) * mm});
            skLineSegment(sketch, "E667", {"start": v(-14.41, 3.48) * mm, "end": v(-14.44, 3.44) * mm});
            skLineSegment(sketch, "E668", {"start": v(-14.44, 3.44) * mm, "end": v(-14.55, 3.34) * mm});
            skLineSegment(sketch, "E669", {"start": v(-14.55, 3.34) * mm, "end": v(-14.7, 3.3) * mm});
            skLineSegment(sketch, "E670", {"start": v(-14.7, 3.3) * mm, "end": v(-14.85, 3.31) * mm});
            skLineSegment(sketch, "E671", {"start": v(-14.85, 3.31) * mm, "end": v(-14.96, 3.32) * mm});
            skLineSegment(sketch, "E672", {"start": v(-14.96, 3.32) * mm, "end": v(-15, 3.32) * mm});
            skLineSegment(sketch, "E673", {"start": v(-15, 3.32) * mm, "end": v(-14.92, 3.22) * mm});
            skLineSegment(sketch, "E674", {"start": v(-14.92, 3.22) * mm, "end": v(-14.47, 2.77) * mm});
            skLineSegment(sketch, "E675", {"start": v(-14.47, 2.77) * mm, "end": v(-14.01, 2.37) * mm});
            skLineSegment(sketch, "E676", {"start": v(-14.01, 2.37) * mm, "end": v(-13.92, 2.3) * mm});
            skLineSegment(sketch, "E677", {"start": v(-13.92, 2.3) * mm, "end": v(-13.94, 2.27) * mm});
            skLineSegment(sketch, "E678", {"start": v(-13.94, 2.27) * mm, "end": v(-14.08, 2.2) * mm});
            skLineSegment(sketch, "E679", {"start": v(-14.08, 2.2) * mm, "end": v(-14.33, 2.13) * mm});
            skLineSegment(sketch, "E680", {"start": v(-14.33, 2.13) * mm, "end": v(-14.4, 2.11) * mm});
            skLineSegment(sketch, "E681", {"start": v(-14.4, 2.11) * mm, "end": v(-14.3, 2) * mm});
            skLineSegment(sketch, "E682", {"start": v(-14.3, 2) * mm, "end": v(-13.96, 1.72) * mm});
            skLineSegment(sketch, "E683", {"start": v(-13.96, 1.72) * mm, "end": v(-13.42, 1.33) * mm});
            skLineSegment(sketch, "E684", {"start": v(-13.42, 1.33) * mm, "end": v(-12.8, 1) * mm});
            skLineSegment(sketch, "E685", {"start": v(-12.8, 1) * mm, "end": v(-12.16, 0.76) * mm});
            skLineSegment(sketch, "E686", {"start": v(-12.16, 0.76) * mm, "end": v(-11.51, 0.67) * mm});
            skLineSegment(sketch, "E687", {"start": v(-11.51, 0.67) * mm, "end": v(-10.9, 0.77) * mm});
            skLineSegment(sketch, "E688", {"start": v(-10.9, 0.77) * mm, "end": v(-10.36, 1.11) * mm});
            skLineSegment(sketch, "E689", {"start": v(-10.36, 1.11) * mm, "end": v(-10, 1.57) * mm});
            skLineSegment(sketch, "E690", {"start": v(-10, 1.57) * mm, "end": v(-9.92, 1.74) * mm});
            skLineSegment(sketch, "E691", {"start": v(-9.92, 1.74) * mm, "end": v(-10.2, 2.08) * mm});
            skLineSegment(sketch, "E692", {"start": v(-10.2, 2.08) * mm, "end": v(-10.95, 3.14) * mm});
            skLineSegment(sketch, "E693", {"start": v(-10.95, 3.14) * mm, "end": v(-11.84, 4.66) * mm});
            skLineSegment(sketch, "E694", {"start": v(-11.84, 4.66) * mm, "end": v(-12.6, 6.28) * mm});
            skLineSegment(sketch, "E695", {"start": v(-12.6, 6.28) * mm, "end": v(-13.11, 7.57) * mm});
            skLineSegment(sketch, "E696", {"start": v(-13.11, 7.57) * mm, "end": v(-13.26, 8) * mm});
            skLineSegment(sketch, "E697", {"start": v(6.91, 3.64) * mm, "end": v(7.08, 3.64) * mm});
            skLineSegment(sketch, "E698", {"start": v(7.08, 3.64) * mm, "end": v(7.57, 3.57) * mm});
            skLineSegment(sketch, "E699", {"start": v(7.57, 3.57) * mm, "end": v(8.2, 3.37) * mm});
            skLineSegment(sketch, "E700", {"start": v(8.2, 3.37) * mm, "end": v(8.78, 3.03) * mm});
            skLineSegment(sketch, "E701", {"start": v(8.78, 3.03) * mm, "end": v(9.18, 2.7) * mm});
            skLineSegment(sketch, "E702", {"start": v(9.18, 2.7) * mm, "end": v(9.3, 2.58) * mm});
            skLineSegment(sketch, "E703", {"start": v(9.3, 2.58) * mm, "end": v(9.41, 2.45) * mm});
            skLineSegment(sketch, "E704", {"start": v(9.41, 2.45) * mm, "end": v(9.71, 2.03) * mm});
            skLineSegment(sketch, "E705", {"start": v(9.71, 2.03) * mm, "end": v(10.02, 1.4) * mm});
            skLineSegment(sketch, "E706", {"start": v(10.02, 1.4) * mm, "end": v(10.21, 0.72) * mm});
            skLineSegment(sketch, "E707", {"start": v(10.21, 0.72) * mm, "end": v(10.28, 0.18) * mm});
            skLineSegment(sketch, "E708", {"start": v(10.28, 0.18) * mm, "end": v(10.28, 0) * mm});
            skLineSegment(sketch, "E709", {"start": v(10.28, 0) * mm, "end": v(10.28, -0.17) * mm});
            skLineSegment(sketch, "E710", {"start": v(10.28, -0.17) * mm, "end": v(10.21, -0.7) * mm});
            skLineSegment(sketch, "E711", {"start": v(10.21, -0.7) * mm, "end": v(10.02, -1.39) * mm});
            skLineSegment(sketch, "E712", {"start": v(10.02, -1.39) * mm, "end": v(9.71, -2.01) * mm});
            skLineSegment(sketch, "E713", {"start": v(9.71, -2.01) * mm, "end": v(9.41, -2.44) * mm});
            skLineSegment(sketch, "E714", {"start": v(9.41, -2.44) * mm, "end": v(9.3, -2.57) * mm});
            skLineSegment(sketch, "E715", {"start": v(9.3, -2.57) * mm, "end": v(9.18, -2.7) * mm});
            skLineSegment(sketch, "E716", {"start": v(9.18, -2.7) * mm, "end": v(8.78, -3.02) * mm});
            skLineSegment(sketch, "E717", {"start": v(8.78, -3.02) * mm, "end": v(8.2, -3.35) * mm});
            skLineSegment(sketch, "E718", {"start": v(8.2, -3.35) * mm, "end": v(7.57, -3.56) * mm});
            skLineSegment(sketch, "E719", {"start": v(7.57, -3.56) * mm, "end": v(7.08, -3.63) * mm});
            skLineSegment(sketch, "E720", {"start": v(7.08, -3.63) * mm, "end": v(6.91, -3.62) * mm});
            skLineSegment(sketch, "E721", {"start": v(6.91, -3.62) * mm, "end": v(6.75, -3.63) * mm});
            skLineSegment(sketch, "E722", {"start": v(6.75, -3.63) * mm, "end": v(6.26, -3.56) * mm});
            skLineSegment(sketch, "E723", {"start": v(6.26, -3.56) * mm, "end": v(5.63, -3.35) * mm});
            skLineSegment(sketch, "E724", {"start": v(5.63, -3.35) * mm, "end": v(5.05, -3.02) * mm});
            skLineSegment(sketch, "E725", {"start": v(5.05, -3.02) * mm, "end": v(4.65, -2.7) * mm});
            skLineSegment(sketch, "E726", {"start": v(4.65, -2.7) * mm, "end": v(4.54, -2.57) * mm});
            skLineSegment(sketch, "E727", {"start": v(4.54, -2.57) * mm, "end": v(4.42, -2.44) * mm});
            skLineSegment(sketch, "E728", {"start": v(4.42, -2.44) * mm, "end": v(4.12, -2.01) * mm});
            skLineSegment(sketch, "E729", {"start": v(4.12, -2.01) * mm, "end": v(3.8, -1.39) * mm});
            skLineSegment(sketch, "E730", {"start": v(3.8, -1.39) * mm, "end": v(3.61, -0.7) * mm});
            skLineSegment(sketch, "E731", {"start": v(3.61, -0.7) * mm, "end": v(3.55, -0.17) * mm});
            skLineSegment(sketch, "E732", {"start": v(3.55, -0.17) * mm, "end": v(3.55, 0) * mm});
            skLineSegment(sketch, "E733", {"start": v(3.55, 0) * mm, "end": v(3.55, 0.18) * mm});
            skLineSegment(sketch, "E734", {"start": v(3.55, 0.18) * mm, "end": v(3.61, 0.72) * mm});
            skLineSegment(sketch, "E735", {"start": v(3.61, 0.72) * mm, "end": v(3.8, 1.4) * mm});
            skLineSegment(sketch, "E736", {"start": v(3.8, 1.4) * mm, "end": v(4.12, 2.03) * mm});
            skLineSegment(sketch, "E737", {"start": v(4.12, 2.03) * mm, "end": v(4.42, 2.45) * mm});
            skLineSegment(sketch, "E738", {"start": v(4.42, 2.45) * mm, "end": v(4.54, 2.58) * mm});
            skLineSegment(sketch, "E739", {"start": v(4.54, 2.58) * mm, "end": v(4.65, 2.7) * mm});
            skLineSegment(sketch, "E740", {"start": v(4.65, 2.7) * mm, "end": v(5.05, 3.03) * mm});
            skLineSegment(sketch, "E741", {"start": v(5.05, 3.03) * mm, "end": v(5.63, 3.37) * mm});
            skLineSegment(sketch, "E742", {"start": v(5.63, 3.37) * mm, "end": v(6.26, 3.57) * mm});
            skLineSegment(sketch, "E743", {"start": v(6.26, 3.57) * mm, "end": v(6.75, 3.64) * mm});
            skLineSegment(sketch, "E744", {"start": v(6.75, 3.64) * mm, "end": v(6.91, 3.64) * mm});
            skLineSegment(sketch, "E745", {"start": v(-2.65, -2.1) * mm, "end": v(-2.56, -1.96) * mm});
            skLineSegment(sketch, "E746", {"start": v(-2.56, -1.96) * mm, "end": v(-2.22, -1.59) * mm});
            skLineSegment(sketch, "E747", {"start": v(-2.22, -1.59) * mm, "end": v(-1.7, -1.2) * mm});
            skLineSegment(sketch, "E748", {"start": v(-1.7, -1.2) * mm, "end": v(-1.1, -0.93) * mm});
            skLineSegment(sketch, "E749", {"start": v(-1.1, -0.93) * mm, "end": v(-0.45, -0.79) * mm});
            skLineSegment(sketch, "E750", {"start": v(-0.45, -0.79) * mm, "end": v(0.24, -0.77) * mm});
            skLineSegment(sketch, "E751", {"start": v(0.24, -0.77) * mm, "end": v(0.95, -0.88) * mm});
            skLineSegment(sketch, "E752", {"start": v(0.95, -0.88) * mm, "end": v(1.66, -1.12) * mm});
            skLineSegment(sketch, "E753", {"start": v(1.66, -1.12) * mm, "end": v(2.18, -1.38) * mm});
            skLineSegment(sketch, "E754", {"start": v(2.18, -1.38) * mm, "end": v(2.34, -1.49) * mm});
            skLineSegment(sketch, "E755", {"start": v(2.34, -1.49) * mm, "end": v(2.5, -1.6) * mm});
            skLineSegment(sketch, "E756", {"start": v(2.5, -1.6) * mm, "end": v(2.95, -1.97) * mm});
            skLineSegment(sketch, "E757", {"start": v(2.95, -1.97) * mm, "end": v(3.45, -2.53) * mm});
            skLineSegment(sketch, "E758", {"start": v(3.45, -2.53) * mm, "end": v(3.83, -3.14) * mm});
            skLineSegment(sketch, "E759", {"start": v(3.83, -3.14) * mm, "end": v(4.08, -3.78) * mm});
            skLineSegment(sketch, "E760", {"start": v(4.08, -3.78) * mm, "end": v(4.21, -4.45) * mm});
            skLineSegment(sketch, "E761", {"start": v(4.21, -4.45) * mm, "end": v(4.2, -5.1) * mm});
            skLineSegment(sketch, "E762", {"start": v(4.2, -5.1) * mm, "end": v(4.06, -5.74) * mm});
            skLineSegment(sketch, "E763", {"start": v(4.06, -5.74) * mm, "end": v(3.85, -6.2) * mm});
            skLineSegment(sketch, "E764", {"start": v(3.85, -6.2) * mm, "end": v(3.76, -6.33) * mm});
            skLineSegment(sketch, "E765", {"start": v(3.76, -6.33) * mm, "end": v(3.67, -6.47) * mm});
            skLineSegment(sketch, "E766", {"start": v(3.67, -6.47) * mm, "end": v(3.34, -6.84) * mm});
            skLineSegment(sketch, "E767", {"start": v(3.34, -6.84) * mm, "end": v(2.82, -7.22) * mm});
            skLineSegment(sketch, "E768", {"start": v(2.82, -7.22) * mm, "end": v(2.22, -7.5) * mm});
            skLineSegment(sketch, "E769", {"start": v(2.22, -7.5) * mm, "end": v(1.56, -7.64) * mm});
            skLineSegment(sketch, "E770", {"start": v(1.56, -7.64) * mm, "end": v(0.87, -7.66) * mm});
            skLineSegment(sketch, "E771", {"start": v(0.87, -7.66) * mm, "end": v(0.16, -7.55) * mm});
            skLineSegment(sketch, "E772", {"start": v(0.16, -7.55) * mm, "end": v(-0.55, -7.3) * mm});
            skLineSegment(sketch, "E773", {"start": v(-0.55, -7.3) * mm, "end": v(-1.07, -7.04) * mm});
            skLineSegment(sketch, "E774", {"start": v(-1.07, -7.04) * mm, "end": v(-1.23, -6.94) * mm});
            skLineSegment(sketch, "E775", {"start": v(-1.23, -6.94) * mm, "end": v(-1.39, -6.83) * mm});
            skLineSegment(sketch, "E776", {"start": v(-1.39, -6.83) * mm, "end": v(-1.84, -6.45) * mm});
            skLineSegment(sketch, "E777", {"start": v(-1.84, -6.45) * mm, "end": v(-2.34, -5.9) * mm});
            skLineSegment(sketch, "E778", {"start": v(-2.34, -5.9) * mm, "end": v(-2.72, -5.29) * mm});
            skLineSegment(sketch, "E779", {"start": v(-2.72, -5.29) * mm, "end": v(-2.97, -4.64) * mm});
            skLineSegment(sketch, "E780", {"start": v(-2.97, -4.64) * mm, "end": v(-3.1, -3.98) * mm});
            skLineSegment(sketch, "E781", {"start": v(-3.1, -3.98) * mm, "end": v(-3.1, -3.32) * mm});
            skLineSegment(sketch, "E782", {"start": v(-3.1, -3.32) * mm, "end": v(-2.94, -2.69) * mm});
            skLineSegment(sketch, "E783", {"start": v(-2.94, -2.69) * mm, "end": v(-2.74, -2.23) * mm});
            skLineSegment(sketch, "E784", {"start": v(-2.74, -2.23) * mm, "end": v(-2.65, -2.1) * mm});
            skLineSegment(sketch, "E785", {"start": v(-2.83, 1.97) * mm, "end": v(-2.74, 1.83) * mm});
            skLineSegment(sketch, "E786", {"start": v(-2.74, 1.83) * mm, "end": v(-2.4, 1.46) * mm});
            skLineSegment(sketch, "E787", {"start": v(-2.4, 1.46) * mm, "end": v(-1.88, 1.07) * mm});
            skLineSegment(sketch, "E788", {"start": v(-1.88, 1.07) * mm, "end": v(-1.28, 0.8) * mm});
            skLineSegment(sketch, "E789", {"start": v(-1.28, 0.8) * mm, "end": v(-0.63, 0.66) * mm});
            skLineSegment(sketch, "E790", {"start": v(-0.63, 0.66) * mm, "end": v(0.07, 0.64) * mm});
            skLineSegment(sketch, "E791", {"start": v(0.07, 0.64) * mm, "end": v(0.77, 0.75) * mm});
            skLineSegment(sketch, "E792", {"start": v(0.77, 0.75) * mm, "end": v(1.48, 0.99) * mm});
            skLineSegment(sketch, "E793", {"start": v(1.48, 0.99) * mm, "end": v(2, 1.25) * mm});
            skLineSegment(sketch, "E794", {"start": v(2, 1.25) * mm, "end": v(2.16, 1.36) * mm});
            skLineSegment(sketch, "E795", {"start": v(2.16, 1.36) * mm, "end": v(2.32, 1.47) * mm});
            skLineSegment(sketch, "E796", {"start": v(2.32, 1.47) * mm, "end": v(2.77, 1.84) * mm});
            skLineSegment(sketch, "E797", {"start": v(2.77, 1.84) * mm, "end": v(3.27, 2.4) * mm});
            skLineSegment(sketch, "E798", {"start": v(3.27, 2.4) * mm, "end": v(3.65, 3) * mm});
            skLineSegment(sketch, "E799", {"start": v(3.65, 3) * mm, "end": v(3.9, 3.66) * mm});
            skLineSegment(sketch, "E800", {"start": v(3.9, 3.66) * mm, "end": v(4.03, 4.32) * mm});
            skLineSegment(sketch, "E801", {"start": v(4.03, 4.32) * mm, "end": v(4.03, 4.98) * mm});
            skLineSegment(sketch, "E802", {"start": v(4.03, 4.98) * mm, "end": v(3.88, 5.61) * mm});
            skLineSegment(sketch, "E803", {"start": v(3.88, 5.61) * mm, "end": v(3.67, 6.06) * mm});
            skLineSegment(sketch, "E804", {"start": v(3.67, 6.06) * mm, "end": v(3.58, 6.2) * mm});
            skLineSegment(sketch, "E805", {"start": v(3.58, 6.2) * mm, "end": v(3.5, 6.34) * mm});
            skLineSegment(sketch, "E806", {"start": v(3.5, 6.34) * mm, "end": v(3.16, 6.7) * mm});
            skLineSegment(sketch, "E807", {"start": v(3.16, 6.7) * mm, "end": v(2.64, 7.1) * mm});
            skLineSegment(sketch, "E808", {"start": v(2.64, 7.1) * mm, "end": v(2.04, 7.36) * mm});
            skLineSegment(sketch, "E809", {"start": v(2.04, 7.36) * mm, "end": v(1.38, 7.5) * mm});
            skLineSegment(sketch, "E810", {"start": v(1.38, 7.5) * mm, "end": v(0.7, 7.53) * mm});
            skLineSegment(sketch, "E811", {"start": v(0.7, 7.53) * mm, "end": v(-0.02, 7.42) * mm});
            skLineSegment(sketch, "E812", {"start": v(-0.02, 7.42) * mm, "end": v(-0.72, 7.18) * mm});
            skLineSegment(sketch, "E813", {"start": v(-0.72, 7.18) * mm, "end": v(-1.25, 6.91) * mm});
            skLineSegment(sketch, "E814", {"start": v(-1.25, 6.91) * mm, "end": v(-1.4, 6.8) * mm});
            skLineSegment(sketch, "E815", {"start": v(-1.4, 6.8) * mm, "end": v(-1.57, 6.7) * mm});
            skLineSegment(sketch, "E816", {"start": v(-1.57, 6.7) * mm, "end": v(-2.02, 6.33) * mm});
            skLineSegment(sketch, "E817", {"start": v(-2.02, 6.33) * mm, "end": v(-2.51, 5.77) * mm});
            skLineSegment(sketch, "E818", {"start": v(-2.51, 5.77) * mm, "end": v(-2.9, 5.16) * mm});
            skLineSegment(sketch, "E819", {"start": v(-2.9, 5.16) * mm, "end": v(-3.15, 4.51) * mm});
            skLineSegment(sketch, "E820", {"start": v(-3.15, 4.51) * mm, "end": v(-3.28, 3.85) * mm});
            skLineSegment(sketch, "E821", {"start": v(-3.28, 3.85) * mm, "end": v(-3.27, 3.2) * mm});
            skLineSegment(sketch, "E822", {"start": v(-3.27, 3.2) * mm, "end": v(-3.12, 2.56) * mm});
            skLineSegment(sketch, "E823", {"start": v(-3.12, 2.56) * mm, "end": v(-2.92, 2.1) * mm});
            skLineSegment(sketch, "E824", {"start": v(-2.92, 2.1) * mm, "end": v(-2.83, 1.97) * mm});
            skLineSegment(sketch, "E825", {"start": v(-1.04, -9.61) * mm, "end": v(-1.05, -9.55) * mm});
            skLineSegment(sketch, "E826", {"start": v(-1.05, -9.55) * mm, "end": v(-1.03, -9.34) * mm});
            skLineSegment(sketch, "E827", {"start": v(-1.03, -9.34) * mm, "end": v(-0.88, -9.13) * mm});
            skLineSegment(sketch, "E828", {"start": v(-0.88, -9.13) * mm, "end": v(-0.58, -8.97) * mm});
            skLineSegment(sketch, "E829", {"start": v(-0.58, -8.97) * mm, "end": v(-0.18, -8.86) * mm});
            skLineSegment(sketch, "E830", {"start": v(-0.18, -8.86) * mm, "end": v(0.3, -8.8) * mm});
            skLineSegment(sketch, "E831", {"start": v(0.3, -8.8) * mm, "end": v(0.87, -8.8) * mm});
            skLineSegment(sketch, "E832", {"start": v(0.87, -8.8) * mm, "end": v(1.47, -8.83) * mm});
            skLineSegment(sketch, "E833", {"start": v(1.47, -8.83) * mm, "end": v(2.09, -8.9) * mm});
            skLineSegment(sketch, "E834", {"start": v(2.09, -8.9) * mm, "end": v(2.7, -9) * mm});
            skLineSegment(sketch, "E835", {"start": v(2.7, -9) * mm, "end": v(3.3, -9.13) * mm});
            skLineSegment(sketch, "E836", {"start": v(3.3, -9.13) * mm, "end": v(3.84, -9.3) * mm});
            skLineSegment(sketch, "E837", {"start": v(3.84, -9.3) * mm, "end": v(4.32, -9.48) * mm});
            skLineSegment(sketch, "E838", {"start": v(4.32, -9.48) * mm, "end": v(4.7, -9.68) * mm});
            skLineSegment(sketch, "E839", {"start": v(4.7, -9.68) * mm, "end": v(4.98, -9.9) * mm});
            skLineSegment(sketch, "E840", {"start": v(4.98, -9.9) * mm, "end": v(5.12, -10.14) * mm});
            skLineSegment(sketch, "E841", {"start": v(5.12, -10.14) * mm, "end": v(5.12, -10.33) * mm});
            skLineSegment(sketch, "E842", {"start": v(5.12, -10.33) * mm, "end": v(5.1, -10.39) * mm});
            skLineSegment(sketch, "E843", {"start": v(5.1, -10.39) * mm, "end": v(5.04, -10.46) * mm});
            skLineSegment(sketch, "E844", {"start": v(5.04, -10.46) * mm, "end": v(4.85, -10.65) * mm});
            skLineSegment(sketch, "E845", {"start": v(4.85, -10.65) * mm, "end": v(4.56, -10.88) * mm});
            skLineSegment(sketch, "E846", {"start": v(4.56, -10.88) * mm, "end": v(4.23, -11.09) * mm});
            skLineSegment(sketch, "E847", {"start": v(4.23, -11.09) * mm, "end": v(3.86, -11.26) * mm});
            skLineSegment(sketch, "E848", {"start": v(3.86, -11.26) * mm, "end": v(3.46, -11.4) * mm});
            skLineSegment(sketch, "E849", {"start": v(3.46, -11.4) * mm, "end": v(3.05, -11.5) * mm});
            skLineSegment(sketch, "E850", {"start": v(3.05, -11.5) * mm, "end": v(2.61, -11.55) * mm});
            skLineSegment(sketch, "E851", {"start": v(2.61, -11.55) * mm, "end": v(2.17, -11.55) * mm});
            skLineSegment(sketch, "E852", {"start": v(2.17, -11.55) * mm, "end": v(1.72, -11.52) * mm});
            skLineSegment(sketch, "E853", {"start": v(1.72, -11.52) * mm, "end": v(1.27, -11.42) * mm});
            skLineSegment(sketch, "E854", {"start": v(1.27, -11.42) * mm, "end": v(0.83, -11.28) * mm});
            skLineSegment(sketch, "E855", {"start": v(0.83, -11.28) * mm, "end": v(0.4, -11.07) * mm});
            skLineSegment(sketch, "E856", {"start": v(0.4, -11.07) * mm, "end": v(0, -10.8) * mm});
            skLineSegment(sketch, "E857", {"start": v(0, -10.8) * mm, "end": v(-0.38, -10.48) * mm});
            skLineSegment(sketch, "E858", {"start": v(-0.38, -10.48) * mm, "end": v(-0.73, -10.08) * mm});
            skLineSegment(sketch, "E859", {"start": v(-0.73, -10.08) * mm, "end": v(-0.97, -9.73) * mm});
            skLineSegment(sketch, "E860", {"start": v(-0.97, -9.73) * mm, "end": v(-1.04, -9.61) * mm});
            skLineSegment(sketch, "E861", {"start": v(-1.13, 9.16) * mm, "end": v(-1.14, 9.1) * mm});
            skLineSegment(sketch, "E862", {"start": v(-1.14, 9.1) * mm, "end": v(-1.12, 8.88) * mm});
            skLineSegment(sketch, "E863", {"start": v(-1.12, 8.88) * mm, "end": v(-0.96, 8.67) * mm});
            skLineSegment(sketch, "E864", {"start": v(-0.96, 8.67) * mm, "end": v(-0.67, 8.51) * mm});
            skLineSegment(sketch, "E865", {"start": v(-0.67, 8.51) * mm, "end": v(-0.27, 8.4) * mm});
            skLineSegment(sketch, "E866", {"start": v(-0.27, 8.4) * mm, "end": v(0.22, 8.35) * mm});
            skLineSegment(sketch, "E867", {"start": v(0.22, 8.35) * mm, "end": v(0.78, 8.34) * mm});
            skLineSegment(sketch, "E868", {"start": v(0.78, 8.34) * mm, "end": v(1.38, 8.37) * mm});
            skLineSegment(sketch, "E869", {"start": v(1.38, 8.37) * mm, "end": v(2, 8.44) * mm});
            skLineSegment(sketch, "E870", {"start": v(2, 8.44) * mm, "end": v(2.61, 8.54) * mm});
            skLineSegment(sketch, "E871", {"start": v(2.61, 8.54) * mm, "end": v(3.2, 8.68) * mm});
            skLineSegment(sketch, "E872", {"start": v(3.2, 8.68) * mm, "end": v(3.76, 8.84) * mm});
            skLineSegment(sketch, "E873", {"start": v(3.76, 8.84) * mm, "end": v(4.23, 9.02) * mm});
            skLineSegment(sketch, "E874", {"start": v(4.23, 9.02) * mm, "end": v(4.62, 9.23) * mm});
            skLineSegment(sketch, "E875", {"start": v(4.62, 9.23) * mm, "end": v(4.9, 9.45) * mm});
            skLineSegment(sketch, "E876", {"start": v(4.9, 9.45) * mm, "end": v(5.03, 9.69) * mm});
            skLineSegment(sketch, "E877", {"start": v(5.03, 9.69) * mm, "end": v(5.03, 9.88) * mm});
            skLineSegment(sketch, "E878", {"start": v(5.03, 9.88) * mm, "end": v(5, 9.93) * mm});
            skLineSegment(sketch, "E879", {"start": v(5, 9.93) * mm, "end": v(4.95, 10) * mm});
            skLineSegment(sketch, "E880", {"start": v(4.95, 10) * mm, "end": v(4.76, 10.2) * mm});
            skLineSegment(sketch, "E881", {"start": v(4.76, 10.2) * mm, "end": v(4.47, 10.42) * mm});
            skLineSegment(sketch, "E882", {"start": v(4.47, 10.42) * mm, "end": v(4.14, 10.63) * mm});
            skLineSegment(sketch, "E883", {"start": v(4.14, 10.63) * mm, "end": v(3.77, 10.8) * mm});
            skLineSegment(sketch, "E884", {"start": v(3.77, 10.8) * mm, "end": v(3.38, 10.94) * mm});
            skLineSegment(sketch, "E885", {"start": v(3.38, 10.94) * mm, "end": v(2.96, 11.03) * mm});
            skLineSegment(sketch, "E886", {"start": v(2.96, 11.03) * mm, "end": v(2.52, 11.09) * mm});
            skLineSegment(sketch, "E887", {"start": v(2.52, 11.09) * mm, "end": v(2.08, 11.1) * mm});
            skLineSegment(sketch, "E888", {"start": v(2.08, 11.1) * mm, "end": v(1.63, 11.06) * mm});
            skLineSegment(sketch, "E889", {"start": v(1.63, 11.06) * mm, "end": v(1.18, 10.97) * mm});
            skLineSegment(sketch, "E890", {"start": v(1.18, 10.97) * mm, "end": v(0.74, 10.82) * mm});
            skLineSegment(sketch, "E891", {"start": v(0.74, 10.82) * mm, "end": v(0.32, 10.62) * mm});
            skLineSegment(sketch, "E892", {"start": v(0.32, 10.62) * mm, "end": v(-0.09, 10.35) * mm});
            skLineSegment(sketch, "E893", {"start": v(-0.09, 10.35) * mm, "end": v(-0.47, 10.02) * mm});
            skLineSegment(sketch, "E894", {"start": v(-0.47, 10.02) * mm, "end": v(-0.82, 9.63) * mm});
            skLineSegment(sketch, "E895", {"start": v(-0.82, 9.63) * mm, "end": v(-1.06, 9.28) * mm});
            skLineSegment(sketch, "E896", {"start": v(-1.06, 9.28) * mm, "end": v(-1.13, 9.16) * mm});
            skLineSegment(sketch, "E897", {"start": v(-6.45, 3.64) * mm, "end": v(-6.5, 3.9) * mm});
            skLineSegment(sketch, "E898", {"start": v(-6.5, 3.9) * mm, "end": v(-6.53, 4.66) * mm});
            skLineSegment(sketch, "E899", {"start": v(-6.53, 4.66) * mm, "end": v(-6.42, 5.62) * mm});
            skLineSegment(sketch, "E900", {"start": v(-6.42, 5.62) * mm, "end": v(-6.13, 6.49) * mm});
            skLineSegment(sketch, "E901", {"start": v(-6.13, 6.49) * mm, "end": v(-5.66, 7.25) * mm});
            skLineSegment(sketch, "E902", {"start": v(-5.66, 7.25) * mm, "end": v(-5.02, 7.86) * mm});
            skLineSegment(sketch, "E903", {"start": v(-5.02, 7.86) * mm, "end": v(-4.23, 8.33) * mm});
            skLineSegment(sketch, "E904", {"start": v(-4.23, 8.33) * mm, "end": v(-3.3, 8.6) * mm});
            skLineSegment(sketch, "E905", {"start": v(-3.3, 8.6) * mm, "end": v(-2.5, 8.69) * mm});
            skLineSegment(sketch, "E906", {"start": v(-2.5, 8.69) * mm, "end": v(-2.22, 8.68) * mm});
            skLineSegment(sketch, "E907", {"start": v(-2.22, 8.68) * mm, "end": v(-2.19, 8.68) * mm});
            skLineSegment(sketch, "E908", {"start": v(-2.19, 8.68) * mm, "end": v(-2.08, 8.6) * mm});
            skLineSegment(sketch, "E909", {"start": v(-2.08, 8.6) * mm, "end": v(-2.06, 8.4) * mm});
            skLineSegment(sketch, "E910", {"start": v(-2.06, 8.4) * mm, "end": v(-2.17, 8.1) * mm});
            skLineSegment(sketch, "E911", {"start": v(-2.17, 8.1) * mm, "end": v(-2.37, 7.7) * mm});
            skLineSegment(sketch, "E912", {"start": v(-2.37, 7.7) * mm, "end": v(-2.65, 7.26) * mm});
            skLineSegment(sketch, "E913", {"start": v(-2.65, 7.26) * mm, "end": v(-3, 6.77) * mm});
            skLineSegment(sketch, "E914", {"start": v(-3, 6.77) * mm, "end": v(-3.4, 6.26) * mm});
            skLineSegment(sketch, "E915", {"start": v(-3.4, 6.26) * mm, "end": v(-3.84, 5.74) * mm});
            skLineSegment(sketch, "E916", {"start": v(-3.84, 5.74) * mm, "end": v(-4.29, 5.23) * mm});
            skLineSegment(sketch, "E917", {"start": v(-4.29, 5.23) * mm, "end": v(-4.73, 4.76) * mm});
            skLineSegment(sketch, "E918", {"start": v(-4.73, 4.76) * mm, "end": v(-5.16, 4.33) * mm});
            skLineSegment(sketch, "E919", {"start": v(-5.16, 4.33) * mm, "end": v(-5.56, 3.98) * mm});
            skLineSegment(sketch, "E920", {"start": v(-5.56, 3.98) * mm, "end": v(-5.9, 3.71) * mm});
            skLineSegment(sketch, "E921", {"start": v(-5.9, 3.71) * mm, "end": v(-6.18, 3.55) * mm});
            skLineSegment(sketch, "E922", {"start": v(-6.18, 3.55) * mm, "end": v(-6.37, 3.52) * mm});
            skLineSegment(sketch, "E923", {"start": v(-6.37, 3.52) * mm, "end": v(-6.45, 3.6) * mm});
            skLineSegment(sketch, "E924", {"start": v(-6.45, 3.6) * mm, "end": v(-6.45, 3.64) * mm});
            skLineSegment(sketch, "E925", {"start": v(-6.54, -4.1) * mm, "end": v(-6.59, -4.36) * mm});
            skLineSegment(sketch, "E926", {"start": v(-6.59, -4.36) * mm, "end": v(-6.62, -5.13) * mm});
            skLineSegment(sketch, "E927", {"start": v(-6.62, -5.13) * mm, "end": v(-6.5, -6.09) * mm});
            skLineSegment(sketch, "E928", {"start": v(-6.5, -6.09) * mm, "end": v(-6.21, -6.96) * mm});
            skLineSegment(sketch, "E929", {"start": v(-6.21, -6.96) * mm, "end": v(-5.75, -7.71) * mm});
            skLineSegment(sketch, "E930", {"start": v(-5.75, -7.71) * mm, "end": v(-5.11, -8.33) * mm});
            skLineSegment(sketch, "E931", {"start": v(-5.11, -8.33) * mm, "end": v(-4.32, -8.8) * mm});
            skLineSegment(sketch, "E932", {"start": v(-4.32, -8.8) * mm, "end": v(-3.39, -9.07) * mm});
            skLineSegment(sketch, "E933", {"start": v(-3.39, -9.07) * mm, "end": v(-2.58, -9.16) * mm});
            skLineSegment(sketch, "E934", {"start": v(-2.58, -9.16) * mm, "end": v(-2.31, -9.15) * mm});
            skLineSegment(sketch, "E935", {"start": v(-2.31, -9.15) * mm, "end": v(-2.27, -9.14) * mm});
            skLineSegment(sketch, "E936", {"start": v(-2.27, -9.14) * mm, "end": v(-2.17, -9.06) * mm});
            skLineSegment(sketch, "E937", {"start": v(-2.17, -9.06) * mm, "end": v(-2.15, -8.86) * mm});
            skLineSegment(sketch, "E938", {"start": v(-2.15, -8.86) * mm, "end": v(-2.26, -8.56) * mm});
            skLineSegment(sketch, "E939", {"start": v(-2.26, -8.56) * mm, "end": v(-2.46, -8.18) * mm});
            skLineSegment(sketch, "E940", {"start": v(-2.46, -8.18) * mm, "end": v(-2.74, -7.73) * mm});
            skLineSegment(sketch, "E941", {"start": v(-2.74, -7.73) * mm, "end": v(-3.1, -7.24) * mm});
            skLineSegment(sketch, "E942", {"start": v(-3.1, -7.24) * mm, "end": v(-3.5, -6.72) * mm});
            skLineSegment(sketch, "E943", {"start": v(-3.5, -6.72) * mm, "end": v(-3.93, -6.2) * mm});
            skLineSegment(sketch, "E944", {"start": v(-3.93, -6.2) * mm, "end": v(-4.37, -5.7) * mm});
            skLineSegment(sketch, "E945", {"start": v(-4.37, -5.7) * mm, "end": v(-4.82, -5.22) * mm});
            skLineSegment(sketch, "E946", {"start": v(-4.82, -5.22) * mm, "end": v(-5.25, -4.8) * mm});
            skLineSegment(sketch, "E947", {"start": v(-5.25, -4.8) * mm, "end": v(-5.65, -4.45) * mm});
            skLineSegment(sketch, "E948", {"start": v(-5.65, -4.45) * mm, "end": v(-5.99, -4.18) * mm});
            skLineSegment(sketch, "E949", {"start": v(-5.99, -4.18) * mm, "end": v(-6.26, -4.02) * mm});
            skLineSegment(sketch, "E950", {"start": v(-6.26, -4.02) * mm, "end": v(-6.46, -4) * mm});
            skLineSegment(sketch, "E951", {"start": v(-6.46, -4) * mm, "end": v(-6.54, -4.07) * mm});
            skLineSegment(sketch, "E952", {"start": v(-6.54, -4.07) * mm, "end": v(-6.54, -4.1) * mm});
            skLineSegment(sketch, "E953", {"start": v(-7.25, -0.08) * mm, "end": v(-7.26, -0.23) * mm});
            skLineSegment(sketch, "E954", {"start": v(-7.26, -0.23) * mm, "end": v(-7.21, -0.7) * mm});
            skLineSegment(sketch, "E955", {"start": v(-7.21, -0.7) * mm, "end": v(-7.07, -1.3) * mm});
            skLineSegment(sketch, "E956", {"start": v(-7.07, -1.3) * mm, "end": v(-6.84, -1.85) * mm});
            skLineSegment(sketch, "E957", {"start": v(-6.84, -1.85) * mm, "end": v(-6.56, -2.35) * mm});
            skLineSegment(sketch, "E958", {"start": v(-6.56, -2.35) * mm, "end": v(-6.23, -2.76) * mm});
            skLineSegment(sketch, "E959", {"start": v(-6.23, -2.76) * mm, "end": v(-5.9, -3.08) * mm});
            skLineSegment(sketch, "E960", {"start": v(-5.9, -3.08) * mm, "end": v(-5.57, -3.29) * mm});
            skLineSegment(sketch, "E961", {"start": v(-5.57, -3.29) * mm, "end": v(-5.34, -3.36) * mm});
            skLineSegment(sketch, "E962", {"start": v(-5.34, -3.36) * mm, "end": v(-5.27, -3.36) * mm});
            skLineSegment(sketch, "E963", {"start": v(-5.27, -3.36) * mm, "end": v(-5.18, -3.36) * mm});
            skLineSegment(sketch, "E964", {"start": v(-5.18, -3.36) * mm, "end": v(-4.93, -3.3) * mm});
            skLineSegment(sketch, "E965", {"start": v(-4.93, -3.3) * mm, "end": v(-4.6, -3.13) * mm});
            skLineSegment(sketch, "E966", {"start": v(-4.6, -3.13) * mm, "end": v(-4.29, -2.84) * mm});
            skLineSegment(sketch, "E967", {"start": v(-4.29, -2.84) * mm, "end": v(-4, -2.46) * mm});
            skLineSegment(sketch, "E968", {"start": v(-4, -2.46) * mm, "end": v(-3.77, -1.98) * mm});
            skLineSegment(sketch, "E969", {"start": v(-3.77, -1.98) * mm, "end": v(-3.58, -1.42) * mm});
            skLineSegment(sketch, "E970", {"start": v(-3.58, -1.42) * mm, "end": v(-3.46, -0.78) * mm});
            skLineSegment(sketch, "E971", {"start": v(-3.46, -0.78) * mm, "end": v(-3.41, -0.25) * mm});
            skLineSegment(sketch, "E972", {"start": v(-3.41, -0.25) * mm, "end": v(-3.4, -0.07) * mm});
            skLineSegment(sketch, "E973", {"start": v(-3.4, -0.07) * mm, "end": v(-3.4, 0.11) * mm});
            skLineSegment(sketch, "E974", {"start": v(-3.4, 0.11) * mm, "end": v(-3.44, 0.65) * mm});
            skLineSegment(sketch, "E975", {"start": v(-3.44, 0.65) * mm, "end": v(-3.53, 1.3) * mm});
            skLineSegment(sketch, "E976", {"start": v(-3.53, 1.3) * mm, "end": v(-3.69, 1.86) * mm});
            skLineSegment(sketch, "E977", {"start": v(-3.69, 1.86) * mm, "end": v(-3.9, 2.34) * mm});
            skLineSegment(sketch, "E978", {"start": v(-3.9, 2.34) * mm, "end": v(-4.14, 2.72) * mm});
            skLineSegment(sketch, "E979", {"start": v(-4.14, 2.72) * mm, "end": v(-4.43, 3) * mm});
            skLineSegment(sketch, "E980", {"start": v(-4.43, 3) * mm, "end": v(-4.75, 3.17) * mm});
            skLineSegment(sketch, "E981", {"start": v(-4.75, 3.17) * mm, "end": v(-5, 3.23) * mm});
            skLineSegment(sketch, "E982", {"start": v(-5, 3.23) * mm, "end": v(-5.09, 3.24) * mm});
            skLineSegment(sketch, "E983", {"start": v(-5.09, 3.24) * mm, "end": v(-5.19, 3.24) * mm});
            skLineSegment(sketch, "E984", {"start": v(-5.19, 3.24) * mm, "end": v(-5.48, 3.16) * mm});
            skLineSegment(sketch, "E985", {"start": v(-5.48, 3.16) * mm, "end": v(-5.87, 2.93) * mm});
            skLineSegment(sketch, "E986", {"start": v(-5.87, 2.93) * mm, "end": v(-6.24, 2.58) * mm});
            skLineSegment(sketch, "E987", {"start": v(-6.24, 2.58) * mm, "end": v(-6.57, 2.14) * mm});
            skLineSegment(sketch, "E988", {"start": v(-6.57, 2.14) * mm, "end": v(-6.85, 1.62) * mm});
            skLineSegment(sketch, "E989", {"start": v(-6.85, 1.62) * mm, "end": v(-7.07, 1.07) * mm});
            skLineSegment(sketch, "E990", {"start": v(-7.07, 1.07) * mm, "end": v(-7.2, 0.49) * mm});
            skLineSegment(sketch, "E991", {"start": v(-7.2, 0.49) * mm, "end": v(-7.25, 0.06) * mm});
            skLineSegment(sketch, "E992", {"start": v(-7.25, 0.06) * mm, "end": v(-7.25, -0.08) * mm});
            skLineSegment(sketch, "E993", {"start": v(11.32, 0.02) * mm, "end": v(11.31, 0.16) * mm});
            skLineSegment(sketch, "E994", {"start": v(11.31, 0.16) * mm, "end": v(11.32, 0.59) * mm});
            skLineSegment(sketch, "E995", {"start": v(11.32, 0.59) * mm, "end": v(11.38, 1.17) * mm});
            skLineSegment(sketch, "E996", {"start": v(11.38, 1.17) * mm, "end": v(11.48, 1.74) * mm});
            skLineSegment(sketch, "E997", {"start": v(11.48, 1.74) * mm, "end": v(11.62, 2.28) * mm});
            skLineSegment(sketch, "E998", {"start": v(11.62, 2.28) * mm, "end": v(11.8, 2.74) * mm});
            skLineSegment(sketch, "E999", {"start": v(11.8, 2.74) * mm, "end": v(12, 3.11) * mm});
            skLineSegment(sketch, "E1000", {"start": v(12, 3.11) * mm, "end": v(12.24, 3.35) * mm});
            skLineSegment(sketch, "E1001", {"start": v(12.24, 3.35) * mm, "end": v(12.43, 3.44) * mm});
            skLineSegment(sketch, "E1002", {"start": v(12.43, 3.44) * mm, "end": v(12.5, 3.44) * mm});
            skLineSegment(sketch, "E1003", {"start": v(12.5, 3.44) * mm, "end": v(12.57, 3.44) * mm});
            skLineSegment(sketch, "E1004", {"start": v(12.57, 3.44) * mm, "end": v(12.8, 3.37) * mm});
            skLineSegment(sketch, "E1005", {"start": v(12.8, 3.37) * mm, "end": v(13.14, 3.15) * mm});
            skLineSegment(sketch, "E1006", {"start": v(13.14, 3.15) * mm, "end": v(13.5, 2.8) * mm});
            skLineSegment(sketch, "E1007", {"start": v(13.5, 2.8) * mm, "end": v(13.87, 2.35) * mm});
            skLineSegment(sketch, "E1008", {"start": v(13.87, 2.35) * mm, "end": v(14.2, 1.8) * mm});
            skLineSegment(sketch, "E1009", {"start": v(14.2, 1.8) * mm, "end": v(14.47, 1.21) * mm});
            skLineSegment(sketch, "E1010", {"start": v(14.47, 1.21) * mm, "end": v(14.65, 0.58) * mm});
            skLineSegment(sketch, "E1011", {"start": v(14.65, 0.58) * mm, "end": v(14.7, 0.09) * mm});
            skLineSegment(sketch, "E1012", {"start": v(14.7, 0.09) * mm, "end": v(14.7, -0.07) * mm});
            skLineSegment(sketch, "E1013", {"start": v(14.7, -0.07) * mm, "end": v(14.71, -0.24) * mm});
            skLineSegment(sketch, "E1014", {"start": v(14.71, -0.24) * mm, "end": v(14.66, -0.75) * mm});
            skLineSegment(sketch, "E1015", {"start": v(14.66, -0.75) * mm, "end": v(14.5, -1.4) * mm});
            skLineSegment(sketch, "E1016", {"start": v(14.5, -1.4) * mm, "end": v(14.25, -2) * mm});
            skLineSegment(sketch, "E1017", {"start": v(14.25, -2) * mm, "end": v(13.93, -2.53) * mm});
            skLineSegment(sketch, "E1018", {"start": v(13.93, -2.53) * mm, "end": v(13.59, -2.99) * mm});
            skLineSegment(sketch, "E1019", {"start": v(13.59, -2.99) * mm, "end": v(13.24, -3.33) * mm});
            skLineSegment(sketch, "E1020", {"start": v(13.24, -3.33) * mm, "end": v(12.94, -3.55) * mm});
            skLineSegment(sketch, "E1021", {"start": v(12.94, -3.55) * mm, "end": v(12.75, -3.63) * mm});
            skLineSegment(sketch, "E1022", {"start": v(12.75, -3.63) * mm, "end": v(12.7, -3.62) * mm});
            skLineSegment(sketch, "E1023", {"start": v(12.7, -3.62) * mm, "end": v(12.62, -3.63) * mm});
            skLineSegment(sketch, "E1024", {"start": v(12.62, -3.63) * mm, "end": v(12.4, -3.53) * mm});
            skLineSegment(sketch, "E1025", {"start": v(12.4, -3.53) * mm, "end": v(12.14, -3.27) * mm});
            skLineSegment(sketch, "E1026", {"start": v(12.14, -3.27) * mm, "end": v(11.9, -2.86) * mm});
            skLineSegment(sketch, "E1027", {"start": v(11.9, -2.86) * mm, "end": v(11.7, -2.35) * mm});
            skLineSegment(sketch, "E1028", {"start": v(11.7, -2.35) * mm, "end": v(11.53, -1.77) * mm});
            skLineSegment(sketch, "E1029", {"start": v(11.53, -1.77) * mm, "end": v(11.4, -1.16) * mm});
            skLineSegment(sketch, "E1030", {"start": v(11.4, -1.16) * mm, "end": v(11.34, -0.55) * mm});
            skLineSegment(sketch, "E1031", {"start": v(11.34, -0.55) * mm, "end": v(11.32, -0.12) * mm});
            skLineSegment(sketch, "E1032", {"start": v(11.32, -0.12) * mm, "end": v(11.32, 0.02) * mm});
            skLineSegment(sketch, "E1033", {"start": v(7.13, -5.36) * mm, "end": v(7.25, -5.27) * mm});
            skLineSegment(sketch, "E1034", {"start": v(7.25, -5.27) * mm, "end": v(7.63, -5) * mm});
            skLineSegment(sketch, "E1035", {"start": v(7.63, -5) * mm, "end": v(8.2, -4.7) * mm});
            skLineSegment(sketch, "E1036", {"start": v(8.2, -4.7) * mm, "end": v(8.8, -4.48) * mm});
            skLineSegment(sketch, "E1037", {"start": v(8.8, -4.48) * mm, "end": v(9.4, -4.33) * mm});
            skLineSegment(sketch, "E1038", {"start": v(9.4, -4.33) * mm, "end": v(9.97, -4.27) * mm});
            skLineSegment(sketch, "E1039", {"start": v(9.97, -4.27) * mm, "end": v(10.49, -4.3) * mm});
            skLineSegment(sketch, "E1040", {"start": v(10.49, -4.3) * mm, "end": v(10.91, -4.46) * mm});
            skLineSegment(sketch, "E1041", {"start": v(10.91, -4.46) * mm, "end": v(11.16, -4.64) * mm});
            skLineSegment(sketch, "E1042", {"start": v(11.16, -4.64) * mm, "end": v(11.22, -4.72) * mm});
            skLineSegment(sketch, "E1043", {"start": v(11.22, -4.72) * mm, "end": v(11.27, -4.8) * mm});
            skLineSegment(sketch, "E1044", {"start": v(11.27, -4.8) * mm, "end": v(11.37, -5.08) * mm});
            skLineSegment(sketch, "E1045", {"start": v(11.37, -5.08) * mm, "end": v(11.45, -5.53) * mm});
            skLineSegment(sketch, "E1046", {"start": v(11.45, -5.53) * mm, "end": v(11.42, -6.04) * mm});
            skLineSegment(sketch, "E1047", {"start": v(11.42, -6.04) * mm, "end": v(11.3, -6.6) * mm});
            skLineSegment(sketch, "E1048", {"start": v(11.3, -6.6) * mm, "end": v(11.06, -7.2) * mm});
            skLineSegment(sketch, "E1049", {"start": v(11.06, -7.2) * mm, "end": v(10.68, -7.8) * mm});
            skLineSegment(sketch, "E1050", {"start": v(10.68, -7.8) * mm, "end": v(10.16, -8.4) * mm});
            skLineSegment(sketch, "E1051", {"start": v(10.16, -8.4) * mm, "end": v(9.66, -8.82) * mm});
            skLineSegment(sketch, "E1052", {"start": v(9.66, -8.82) * mm, "end": v(9.48, -8.95) * mm});
            skLineSegment(sketch, "E1053", {"start": v(9.48, -8.95) * mm, "end": v(9.33, -9.03) * mm});
            skLineSegment(sketch, "E1054", {"start": v(9.33, -9.03) * mm, "end": v(8.84, -9.25) * mm});
            skLineSegment(sketch, "E1055", {"start": v(8.84, -9.25) * mm, "end": v(8.22, -9.47) * mm});
            skLineSegment(sketch, "E1056", {"start": v(8.22, -9.47) * mm, "end": v(7.62, -9.6) * mm});
            skLineSegment(sketch, "E1057", {"start": v(7.62, -9.6) * mm, "end": v(7.06, -9.64) * mm});
            skLineSegment(sketch, "E1058", {"start": v(7.06, -9.64) * mm, "end": v(6.55, -9.6) * mm});
            skLineSegment(sketch, "E1059", {"start": v(6.55, -9.6) * mm, "end": v(6.12, -9.5) * mm});
            skLineSegment(sketch, "E1060", {"start": v(6.12, -9.5) * mm, "end": v(5.78, -9.33) * mm});
            skLineSegment(sketch, "E1061", {"start": v(5.78, -9.33) * mm, "end": v(5.58, -9.17) * mm});
            skLineSegment(sketch, "E1062", {"start": v(5.58, -9.17) * mm, "end": v(5.53, -9.1) * mm});
            skLineSegment(sketch, "E1063", {"start": v(5.53, -9.1) * mm, "end": v(5.47, -9.02) * mm});
            skLineSegment(sketch, "E1064", {"start": v(5.47, -9.02) * mm, "end": v(5.37, -8.7) * mm});
            skLineSegment(sketch, "E1065", {"start": v(5.37, -8.7) * mm, "end": v(5.33, -8.27) * mm});
            skLineSegment(sketch, "E1066", {"start": v(5.33, -8.27) * mm, "end": v(5.4, -7.8) * mm});
            skLineSegment(sketch, "E1067", {"start": v(5.4, -7.8) * mm, "end": v(5.58, -7.3) * mm});
            skLineSegment(sketch, "E1068", {"start": v(5.58, -7.3) * mm, "end": v(5.85, -6.8) * mm});
            skLineSegment(sketch, "E1069", {"start": v(5.85, -6.8) * mm, "end": v(6.2, -6.31) * mm});
            skLineSegment(sketch, "E1070", {"start": v(6.2, -6.31) * mm, "end": v(6.64, -5.83) * mm});
            skLineSegment(sketch, "E1071", {"start": v(6.64, -5.83) * mm, "end": v(7, -5.47) * mm});
            skLineSegment(sketch, "E1072", {"start": v(7, -5.47) * mm, "end": v(7.13, -5.36) * mm});
            skLineSegment(sketch, "E1073", {"start": v(6.73, 5.2) * mm, "end": v(6.86, 5.1) * mm});
            skLineSegment(sketch, "E1074", {"start": v(6.86, 5.1) * mm, "end": v(7.27, 4.8) * mm});
            skLineSegment(sketch, "E1075", {"start": v(7.27, 4.8) * mm, "end": v(7.88, 4.47) * mm});
            skLineSegment(sketch, "E1076", {"start": v(7.88, 4.47) * mm, "end": v(8.52, 4.2) * mm});
            skLineSegment(sketch, "E1077", {"start": v(8.52, 4.2) * mm, "end": v(9.18, 4) * mm});
            skLineSegment(sketch, "E1078", {"start": v(9.18, 4) * mm, "end": v(9.8, 3.9) * mm});
            skLineSegment(sketch, "E1079", {"start": v(9.8, 3.9) * mm, "end": v(10.38, 3.91) * mm});
            skLineSegment(sketch, "E1080", {"start": v(10.38, 3.91) * mm, "end": v(10.86, 4.03) * mm});
            skLineSegment(sketch, "E1081", {"start": v(10.86, 4.03) * mm, "end": v(11.15, 4.2) * mm});
            skLineSegment(sketch, "E1082", {"start": v(11.15, 4.2) * mm, "end": v(11.22, 4.27) * mm});
            skLineSegment(sketch, "E1083", {"start": v(11.22, 4.27) * mm, "end": v(11.28, 4.35) * mm});
            skLineSegment(sketch, "E1084", {"start": v(11.28, 4.35) * mm, "end": v(11.4, 4.62) * mm});
            skLineSegment(sketch, "E1085", {"start": v(11.4, 4.62) * mm, "end": v(11.52, 5.08) * mm});
            skLineSegment(sketch, "E1086", {"start": v(11.52, 5.08) * mm, "end": v(11.53, 5.61) * mm});
            skLineSegment(sketch, "E1087", {"start": v(11.53, 5.61) * mm, "end": v(11.43, 6.2) * mm});
            skLineSegment(sketch, "E1088", {"start": v(11.43, 6.2) * mm, "end": v(11.2, 6.83) * mm});
            skLineSegment(sketch, "E1089", {"start": v(11.2, 6.83) * mm, "end": v(10.83, 7.47) * mm});
            skLineSegment(sketch, "E1090", {"start": v(10.83, 7.47) * mm, "end": v(10.3, 8.1) * mm});
            skLineSegment(sketch, "E1091", {"start": v(10.3, 8.1) * mm, "end": v(9.77, 8.58) * mm});
            skLineSegment(sketch, "E1092", {"start": v(9.77, 8.58) * mm, "end": v(9.58, 8.71) * mm});
            skLineSegment(sketch, "E1093", {"start": v(9.58, 8.71) * mm, "end": v(9.45, 8.82) * mm});
            skLineSegment(sketch, "E1094", {"start": v(9.45, 8.82) * mm, "end": v(9, 9.07) * mm});
            skLineSegment(sketch, "E1095", {"start": v(9, 9.07) * mm, "end": v(8.35, 9.3) * mm});
            skLineSegment(sketch, "E1096", {"start": v(8.35, 9.3) * mm, "end": v(7.69, 9.41) * mm});
            skLineSegment(sketch, "E1097", {"start": v(7.69, 9.41) * mm, "end": v(7.02, 9.43) * mm});
            skLineSegment(sketch, "E1098", {"start": v(7.02, 9.43) * mm, "end": v(6.4, 9.37) * mm});
            skLineSegment(sketch, "E1099", {"start": v(6.4, 9.37) * mm, "end": v(5.84, 9.23) * mm});
            skLineSegment(sketch, "E1100", {"start": v(5.84, 9.23) * mm, "end": v(5.39, 9.05) * mm});
            skLineSegment(sketch, "E1101", {"start": v(5.39, 9.05) * mm, "end": v(5.14, 8.89) * mm});
            skLineSegment(sketch, "E1102", {"start": v(5.14, 8.89) * mm, "end": v(5.07, 8.82) * mm});
            skLineSegment(sketch, "E1103", {"start": v(5.07, 8.82) * mm, "end": v(5, 8.74) * mm});
            skLineSegment(sketch, "E1104", {"start": v(5, 8.74) * mm, "end": v(4.87, 8.44) * mm});
            skLineSegment(sketch, "E1105", {"start": v(4.87, 8.44) * mm, "end": v(4.81, 8.03) * mm});
            skLineSegment(sketch, "E1106", {"start": v(4.81, 8.03) * mm, "end": v(4.89, 7.6) * mm});
            skLineSegment(sketch, "E1107", {"start": v(4.89, 7.6) * mm, "end": v(5.08, 7.13) * mm});
            skLineSegment(sketch, "E1108", {"start": v(5.08, 7.13) * mm, "end": v(5.37, 6.66) * mm});
            skLineSegment(sketch, "E1109", {"start": v(5.37, 6.66) * mm, "end": v(5.75, 6.17) * mm});
            skLineSegment(sketch, "E1110", {"start": v(5.75, 6.17) * mm, "end": v(6.21, 5.69) * mm});
            skLineSegment(sketch, "E1111", {"start": v(6.21, 5.69) * mm, "end": v(6.6, 5.32) * mm});
            skLineSegment(sketch, "E1112", {"start": v(6.6, 5.32) * mm, "end": v(6.73, 5.2) * mm});
            skLineSegment(sketch, "E1113", {"start": v(6.73, 5.2) * mm, "end": v(6.73, 5.2) * mm});
            skSolve(sketch);
        }
        {
            var Q0;
            Q0=qSketchRegion(id+"F0",true);
            var Q1;
            Q1=makeQuery(id+"F0.imprint","IMPRINT",FACE,{"disambiguationData":[TD([[makeQuery(id+"F0.imprint","IMPRINT",EDGE,{"derivedFrom":sQuery(id+"F0.wireOp",EDGE,"E1")}),-1.0]])]});
            var Q2;
            Q2=makeQuery(id+"F0.imprint","IMPRINT",FACE,{"disambiguationData":[TD([[makeQuery(id+"F0.imprint","IMPRINT",EDGE,{"derivedFrom":sQuery(id+"F0.wireOp",EDGE,"E1")}),1.0]])]});
            var Q3;
            Q3=makeQuery(id+"F0.imprint","IMPRINT",FACE,{"disambiguationData":[TD([[makeQuery(id+"F0.imprint","IMPRINT",EDGE,{"derivedFrom":sQuery(id+"F0.wireOp",EDGE,"E4")}),1.0]])]});
            var Q4;
            Q4=makeQuery(id+"F0.imprint","IMPRINT",FACE,{"disambiguationData":[TD([[makeQuery(id+"F0.imprint","IMPRINT",EDGE,{"derivedFrom":sQuery(id+"F0.wireOp",EDGE,"E4")}),-1.0]])]});
            var Q5;
            Q5=makeQuery(id+"F0.imprint","IMPRINT",FACE,{"disambiguationData":[TD([[makeQuery(id+"F0.imprint","IMPRINT",EDGE,{"derivedFrom":sQuery(id+"F0.wireOp",EDGE,"E3")}),-1.0]])]});
            var Q6;
            Q6=makeQuery(id+"F0.imprint","IMPRINT",FACE,{"disambiguationData":[TD([[makeQuery(id+"F0.imprint","IMPRINT",EDGE,{"derivedFrom":sQuery(id+"F0.wireOp",EDGE,"E3")}),1.0]])]});
            var Q7;
            Q7=makeQuery(id+"F0.imprint","IMPRINT",FACE,{"disambiguationData":[TD([[makeQuery(id+"F0.imprint","IMPRINT",EDGE,{"derivedFrom":sQuery(id+"F0.wireOp",EDGE,"E2")}),-1.0]])]});
            var Q8;
            Q8=makeQuery(id+"F0.imprint","IMPRINT",FACE,{"disambiguationData":[TD([[makeQuery(id+"F0.imprint","IMPRINT",EDGE,{"derivedFrom":sQuery(id+"F0.wireOp",EDGE,"E2")}),1.0]])]});
            extrude(context, id + "F2", {"entities" : qUnion([Q0, Q1, Q2, Q3, Q4, Q5, Q6, Q7, Q8]), "depth" : 7.6 * mm, "offsetDistance" : 25 * mm, "hasSecondDirection" : true, "secondDirectionOppositeDirection" : false, "secondDirectionDepth" : 6.1 * mm});
        }
        {
            var Q0;
            Q0=makeQuery(id+"F0.imprint","IMPRINT",FACE,{"disambiguationData":[TD([[makeQuery(id+"F0.imprint","IMPRINT",EDGE,{"derivedFrom":sQuery(id+"F0.wireOp",EDGE,"E1")}),-1.0]])]});
            var Q1;
            Q1=makeQuery(id+"F0.imprint","IMPRINT",FACE,{"disambiguationData":[TD([[makeQuery(id+"F0.imprint","IMPRINT",EDGE,{"derivedFrom":sQuery(id+"F0.wireOp",EDGE,"E4")}),-1.0]])]});
            var Q2;
            Q2=makeQuery(id+"F0.imprint","IMPRINT",FACE,{"disambiguationData":[TD([[makeQuery(id+"F0.imprint","IMPRINT",EDGE,{"derivedFrom":sQuery(id+"F0.wireOp",EDGE,"E3")}),-1.0]])]});
            var Q3;
            Q3=makeQuery(id+"F0.imprint","IMPRINT",FACE,{"disambiguationData":[TD([[makeQuery(id+"F0.imprint","IMPRINT",EDGE,{"derivedFrom":sQuery(id+"F0.wireOp",EDGE,"E2")}),-1.0]])]});
            var Q4;
            Q4=sQuery(id+"F0.wireOp",EDGE,"E5");
            var Q5;
            Q5=sQuery(id+"F0.wireOp",EDGE,"E1");
            extrude(context, id + "F3", {"entities" : qUnion([Q0, Q1, Q2, Q3]), "operationType" : NewBodyOperationType.ADD, "surfaceEntities" : qUnion([Q4, Q5]), "depth" : 6.1 * mm, "offsetDistance" : 25 * mm, "hasSecondDirection" : true, "secondDirectionOppositeDirection" : false, "secondDirectionDepth" : 3 * mm});
        }
        {
            var Q0;
            Q0=qSketchRegion(id+"F1",true);
            extrude(context, id + "F4", {"entities" : qUnion([Q0]), "operationType" : NewBodyOperationType.REMOVE, "depth" : 8 * mm, "offsetDistance" : 25 * mm, "hasSecondDirection" : true, "secondDirectionOppositeDirection" : false, "secondDirectionDepth" : 6.8 * mm});
        }
    });
